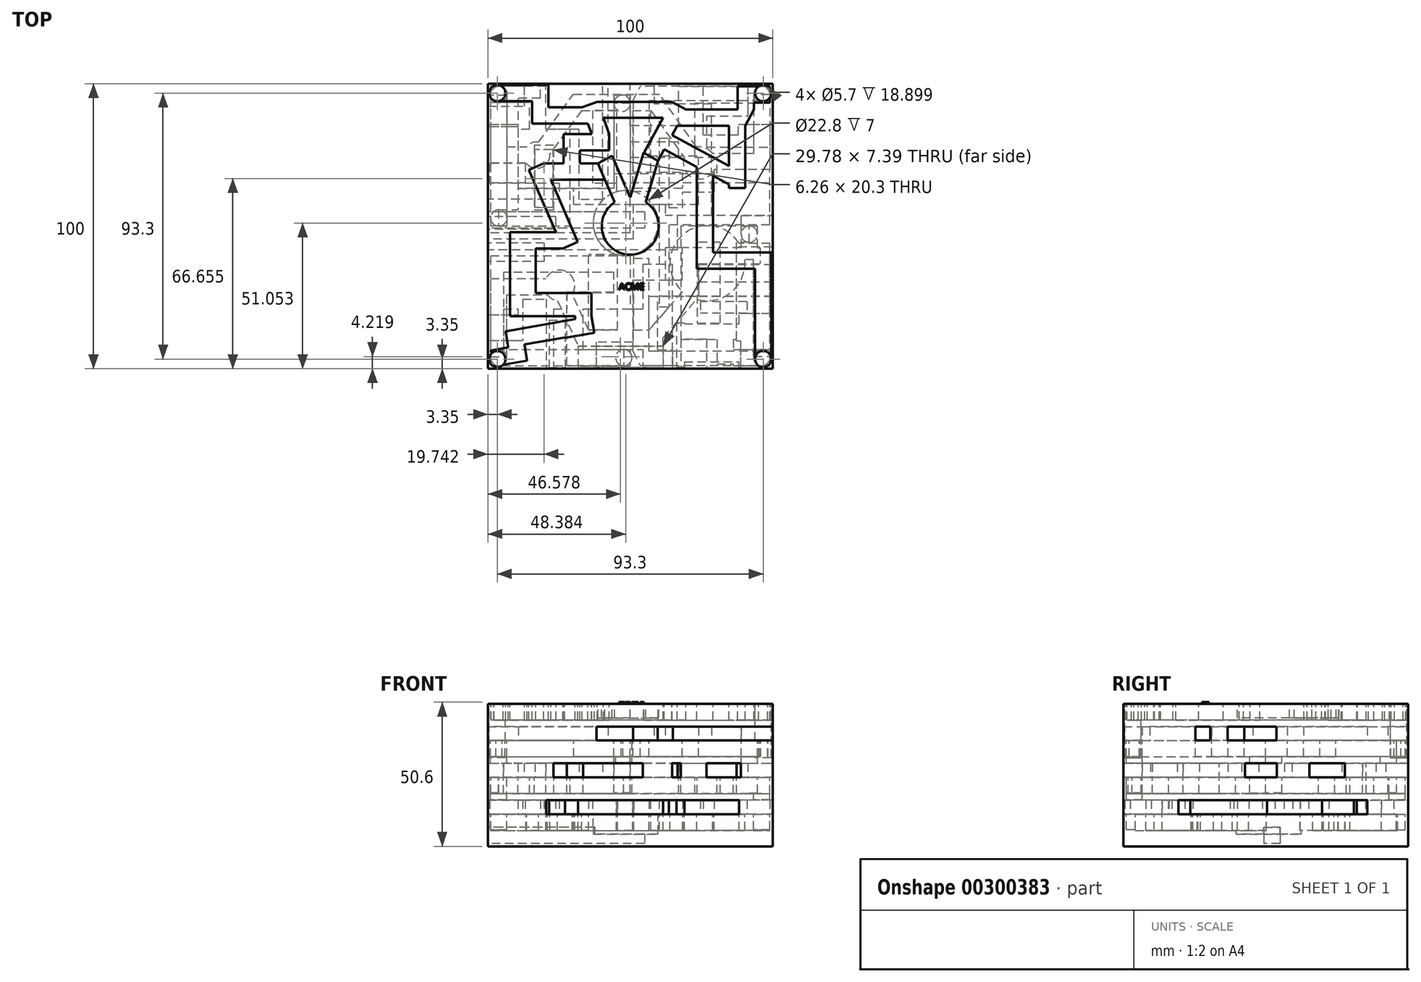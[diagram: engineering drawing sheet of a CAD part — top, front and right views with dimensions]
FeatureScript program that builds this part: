
annotation { "Feature Type Name" : "Feature", "Feature Type Description" : "" }
export const myFeature = defineFeature(function(context is Context, id is Id, definition is map)
    precondition{}
    {
        {
            var Q0;
            Q0=qCreatedBy(makeId("Top.planeOp"),FACE);
            var sketch = newSketch(context, id + "F0", { "sketchPlane" : qUnion([Q0])});
            skLineSegment(sketch, "E0.bottom", {"start": v(-50, 50) * mm, "end": v(50, 50) * mm});
            skLineSegment(sketch, "E0.top", {"start": v(-50, -50) * mm, "end": v(50, -50) * mm});
            skLineSegment(sketch, "E0.left", {"start": v(-50, 50) * mm, "end": v(-50, -50) * mm});
            skLineSegment(sketch, "E0.right", {"start": v(50, 50) * mm, "end": v(50, -50) * mm});
            skPoint(sketch, "E0.middle", {"position": v(0, 0) * mm});
            skSolve(sketch);
        }
        {
            var Q0;
            Q0 = qSketchRegion(id + "F0", true);
            extrude(context, id + "F1", {"entities" : qUnion([Q0]), "oppositeDirection" : true, "depth" : 50 * mm});
        }
        {
            var Q0;
            Q0=makeQuery(id+"F1.opExtrude","CAP_FACE",FACE,{"disambiguationData":[OSD([sQuery(id+"F0.wireOp",EDGE,"E0.bottom"),sQuery(id+"F0.wireOp",EDGE,"E0.top"),sQuery(id+"F0.wireOp",EDGE,"E0.left"),sQuery(id+"F0.wireOp",EDGE,"E0.right")])],"isStart":true});
            var sketch = newSketch(context, id + "F2", { "sketchPlane" : qUnion([Q0])});
            skCircle(sketch, "E1", {"center": v(0, 0) * mm, "radius": 10 * mm});
            skSolve(sketch);
        }
        {
            var Q0;
            Q0 = qSketchRegion(id + "F2", true);
            extrude(context, id + "F3", {"entities" : qUnion([Q0]), "operationType" : NewBodyOperationType.REMOVE, "oppositeDirection" : true, "depth" : 5 * mm});
        }
        {
            var Q0;
            Q0=makeQuery(id+"F1.opExtrude","CAP_FACE",FACE,{"disambiguationData":[OSD([sQuery(id+"F0.wireOp",EDGE,"E0.bottom"),sQuery(id+"F0.wireOp",EDGE,"E0.top"),sQuery(id+"F0.wireOp",EDGE,"E0.left"),sQuery(id+"F0.wireOp",EDGE,"E0.right")])],"isStart":true});
            var sketch = newSketch(context, id + "F4", { "sketchPlane" : qUnion([Q0])});
            skLineSegment(sketch, "E2", {"start": v(0, 10) * mm, "end": v(-6.36, 24.68) * mm});
            skLineSegment(sketch, "E3", {"start": v(0, 10) * mm, "end": v(4.66, 25.69) * mm});
            skLineSegment(sketch, "E4", {"start": v(4.66, 25.69) * mm, "end": v(9.78, 22.9) * mm});
            skLineSegment(sketch, "E5", {"start": v(9.78, 22.9) * mm, "end": v(5.46, 8.38) * mm});
            skLineSegment(sketch, "E6", {"start": v(5.46, 8.38) * mm, "end": v(0, 10) * mm});
            skLineSegment(sketch, "E7", {"start": v(-6.36, 24.68) * mm, "end": v(-11.36, 21.94) * mm});
            skLineSegment(sketch, "E8", {"start": v(-11.36, 21.94) * mm, "end": v(-5.46, 8.38) * mm});
            skLineSegment(sketch, "E9", {"start": v(-5.46, 8.38) * mm, "end": v(0, 10) * mm});
            skSolve(sketch);
        }
        {
            var Q0;
            Q0 = qSketchRegion(id + "F4", true);
            extrude(context, id + "F5", {"entities" : qUnion([Q0]), "operationType" : NewBodyOperationType.REMOVE, "oppositeDirection" : true, "depth" : 5 * mm});
        }
        {
            var Q0;
            Q0=makeQuery(id+"F1.opExtrude","CAP_FACE",FACE,{"disambiguationData":[OSD([sQuery(id+"F0.wireOp",EDGE,"E0.bottom"),sQuery(id+"F0.wireOp",EDGE,"E0.top"),sQuery(id+"F0.wireOp",EDGE,"E0.left"),sQuery(id+"F0.wireOp",EDGE,"E0.right")])],"isStart":true});
            var sketch = newSketch(context, id + "F6", { "sketchPlane" : qUnion([Q0])});
            skLineSegment(sketch, "E10.bottom", {"start": v(-11.36, 21.94) * mm, "end": v(-30.36, 21.94) * mm});
            skLineSegment(sketch, "E10.top", {"start": v(-8.88, 16.24) * mm, "end": v(-27.88, 16.24) * mm});
            skLineSegment(sketch, "E10.left", {"start": v(-11.36, 21.94) * mm, "end": v(-8.88, 16.24) * mm});
            skLineSegment(sketch, "E10.right", {"start": v(-30.36, 21.94) * mm, "end": v(-27.88, 16.24) * mm});
            skLineSegment(sketch, "E11.bottom", {"start": v(-23.36, 21.94) * mm, "end": v(-17.66, 21.94) * mm});
            skLineSegment(sketch, "E11.top", {"start": v(-23.36, 32.25) * mm, "end": v(-17.66, 32.25) * mm});
            skLineSegment(sketch, "E11.left", {"start": v(-23.36, 21.94) * mm, "end": v(-23.36, 32.25) * mm});
            skLineSegment(sketch, "E11.right", {"start": v(-17.66, 21.94) * mm, "end": v(-17.66, 32.25) * mm});
            skLineSegment(sketch, "E12.bottom", {"start": v(-17.66, 32.25) * mm, "end": v(-7.41, 32.25) * mm});
            skLineSegment(sketch, "E12.top", {"start": v(-17.66, 26.55) * mm, "end": v(-7.41, 26.55) * mm});
            skLineSegment(sketch, "E12.left", {"start": v(-17.66, 32.25) * mm, "end": v(-17.66, 26.55) * mm});
            skLineSegment(sketch, "E12.right", {"start": v(-7.41, 32.25) * mm, "end": v(-7.41, 26.55) * mm});
            skLineSegment(sketch, "E13.bottom", {"start": v(-7.41, 32.25) * mm, "end": v(-12.77, 30.3) * mm});
            skLineSegment(sketch, "E13.top", {"start": v(-11.56, 43.65) * mm, "end": v(-16.92, 41.7) * mm});
            skLineSegment(sketch, "E13.left", {"start": v(-7.41, 32.25) * mm, "end": v(-11.56, 43.65) * mm});
            skLineSegment(sketch, "E13.right", {"start": v(-12.77, 30.3) * mm, "end": v(-16.92, 41.7) * mm});
            skLineSegment(sketch, "E14.bottom", {"start": v(-16.92, 41.7) * mm, "end": v(-31.14, 41.7) * mm});
            skLineSegment(sketch, "E14.top", {"start": v(-14.84, 36) * mm, "end": v(-29.06, 36) * mm});
            skLineSegment(sketch, "E14.left", {"start": v(-16.92, 41.7) * mm, "end": v(-14.84, 36) * mm});
            skLineSegment(sketch, "E14.right", {"start": v(-31.14, 41.7) * mm, "end": v(-29.06, 36) * mm});
            skLineSegment(sketch, "E15.bottom", {"start": v(-28.72, 36) * mm, "end": v(-34.42, 36) * mm});
            skLineSegment(sketch, "E15.top", {"start": v(-28.72, 49.5) * mm, "end": v(-34.42, 49.5) * mm});
            skLineSegment(sketch, "E15.left", {"start": v(-28.72, 36) * mm, "end": v(-28.72, 49.5) * mm});
            skLineSegment(sketch, "E15.right", {"start": v(-34.42, 36) * mm, "end": v(-34.42, 49.5) * mm});
            skLineSegment(sketch, "E16.bottom", {"start": v(-47.8, 49.5) * mm, "end": v(-34.42, 49.5) * mm});
            skLineSegment(sketch, "E16.top", {"start": v(-47.8, 43.8) * mm, "end": v(-34.42, 43.8) * mm});
            skLineSegment(sketch, "E16.left", {"start": v(-47.8, 49.5) * mm, "end": v(-47.8, 43.8) * mm});
            skLineSegment(sketch, "E16.right", {"start": v(-34.42, 49.5) * mm, "end": v(-34.42, 43.8) * mm});
            skLineSegment(sketch, "E17.bottom", {"start": v(-30.36, 21.94) * mm, "end": v(-35.59, 19.66) * mm});
            skLineSegment(sketch, "E17.top", {"start": v(-18.4, -5.57) * mm, "end": v(-23.62, -7.85) * mm});
            skLineSegment(sketch, "E17.left", {"start": v(-30.36, 21.94) * mm, "end": v(-18.4, -5.57) * mm});
            skLineSegment(sketch, "E17.right", {"start": v(-35.59, 19.66) * mm, "end": v(-23.62, -7.85) * mm});
            skLineSegment(sketch, "E18.bottom", {"start": v(-23.62, -7.85) * mm, "end": v(-42.16, -7.85) * mm});
            skLineSegment(sketch, "E18.top", {"start": v(-23.62, -2.15) * mm, "end": v(-42.16, -2.15) * mm});
            skLineSegment(sketch, "E18.left", {"start": v(-23.62, -7.85) * mm, "end": v(-23.62, -2.15) * mm});
            skLineSegment(sketch, "E18.right", {"start": v(-42.16, -7.85) * mm, "end": v(-42.16, -2.15) * mm});
            skLineSegment(sketch, "E19.bottom", {"start": v(-42.16, -7.85) * mm, "end": v(-33.16, -7.85) * mm});
            skLineSegment(sketch, "E19.top", {"start": v(-42.16, -31.6) * mm, "end": v(-33.16, -31.6) * mm});
            skLineSegment(sketch, "E19.left", {"start": v(-42.16, -7.85) * mm, "end": v(-42.16, -31.6) * mm});
            skLineSegment(sketch, "E19.right", {"start": v(-33.16, -7.85) * mm, "end": v(-33.16, -31.6) * mm});
            skLineSegment(sketch, "E20.bottom", {"start": v(-33.16, -23.52) * mm, "end": v(-13.61, -23.52) * mm});
            skLineSegment(sketch, "E20.top", {"start": v(-33.16, -31.6) * mm, "end": v(-13.61, -31.6) * mm});
            skLineSegment(sketch, "E20.left", {"start": v(-33.16, -23.52) * mm, "end": v(-33.16, -31.6) * mm});
            skLineSegment(sketch, "E20.right", {"start": v(-13.61, -23.52) * mm, "end": v(-13.61, -31.6) * mm});
            skLineSegment(sketch, "E21.bottom", {"start": v(-13.61, -31.6) * mm, "end": v(-24.04, -33.45) * mm});
            skLineSegment(sketch, "E21.top", {"start": v(-12.58, -37.43) * mm, "end": v(-23.02, -39.27) * mm});
            skLineSegment(sketch, "E21.left", {"start": v(-13.61, -31.6) * mm, "end": v(-12.58, -37.43) * mm});
            skLineSegment(sketch, "E21.right", {"start": v(-24.04, -33.45) * mm, "end": v(-23.02, -39.27) * mm});
            skLineSegment(sketch, "E22.bottom", {"start": v(-13.61, -31.6) * mm, "end": v(-19.31, -31.6) * mm});
            skLineSegment(sketch, "E22.top", {"start": v(-13.61, -32.61) * mm, "end": v(-19.31, -32.61) * mm});
            skLineSegment(sketch, "E22.left", {"start": v(-13.61, -31.6) * mm, "end": v(-13.61, -32.61) * mm});
            skLineSegment(sketch, "E22.right", {"start": v(-19.31, -31.6) * mm, "end": v(-19.31, -32.61) * mm});
            skLineSegment(sketch, "E23.bottom", {"start": v(-24.04, -33.45) * mm, "end": v(-43.78, -36.92) * mm});
            skLineSegment(sketch, "E23.top", {"start": v(-23.05, -39.06) * mm, "end": v(-42.79, -42.54) * mm});
            skLineSegment(sketch, "E23.left", {"start": v(-24.04, -33.45) * mm, "end": v(-23.05, -39.06) * mm});
            skLineSegment(sketch, "E23.right", {"start": v(-43.78, -36.92) * mm, "end": v(-42.79, -42.54) * mm});
            skLineSegment(sketch, "E24.bottom", {"start": v(-42.79, -42.54) * mm, "end": v(-37.17, -41.55) * mm});
            skLineSegment(sketch, "E24.top", {"start": v(-41.8, -48.15) * mm, "end": v(-36.18, -47.16) * mm});
            skLineSegment(sketch, "E24.left", {"start": v(-42.79, -42.54) * mm, "end": v(-41.8, -48.15) * mm});
            skLineSegment(sketch, "E24.right", {"start": v(-37.17, -41.55) * mm, "end": v(-36.18, -47.16) * mm});
            skLineSegment(sketch, "E25.bottom", {"start": v(-41.8, -48.15) * mm, "end": v(-47.94, -49.24) * mm});
            skLineSegment(sketch, "E25.top", {"start": v(-42.79, -42.54) * mm, "end": v(-48.93, -43.62) * mm});
            skLineSegment(sketch, "E25.left", {"start": v(-41.8, -48.15) * mm, "end": v(-42.79, -42.54) * mm});
            skLineSegment(sketch, "E25.right", {"start": v(-47.94, -49.24) * mm, "end": v(-48.93, -43.62) * mm});
            skLineSegment(sketch, "E26.bottom", {"start": v(9.78, 22.9) * mm, "end": v(19.57, 40.93) * mm});
            skLineSegment(sketch, "E26.top", {"start": v(4.77, 25.63) * mm, "end": v(14.56, 43.65) * mm});
            skLineSegment(sketch, "E26.left", {"start": v(9.78, 22.9) * mm, "end": v(4.77, 25.63) * mm});
            skLineSegment(sketch, "E26.right", {"start": v(19.57, 40.93) * mm, "end": v(14.56, 43.65) * mm});
            skPoint(sketch, "E27.oppositeSnap0", {"position": v(-9.49, 37.95) * mm});
            skLineSegment(sketch, "E27.bottom", {"start": v(14.56, 43.65) * mm, "end": v(-11.56, 43.65) * mm});
            skLineSegment(sketch, "E27.top", {"start": v(11.47, 37.95) * mm, "end": v(-9.49, 37.95) * mm});
            skLineSegment(sketch, "E27.left", {"start": v(14.56, 43.65) * mm, "end": v(11.47, 37.95) * mm});
            skLineSegment(sketch, "E27.right", {"start": v(-11.56, 43.65) * mm, "end": v(-9.49, 37.95) * mm});
            skLineSegment(sketch, "E28.bottom", {"start": v(19.57, 40.93) * mm, "end": v(43.44, 40.93) * mm});
            skLineSegment(sketch, "E28.top", {"start": v(16.47, 35.23) * mm, "end": v(40.35, 35.23) * mm});
            skLineSegment(sketch, "E28.left", {"start": v(19.57, 40.93) * mm, "end": v(16.47, 35.23) * mm});
            skLineSegment(sketch, "E28.right", {"start": v(43.44, 40.93) * mm, "end": v(40.35, 35.23) * mm});
            skLineSegment(sketch, "E29.bottom", {"start": v(40.35, 35.23) * mm, "end": v(34.65, 35.23) * mm});
            skLineSegment(sketch, "E29.top", {"start": v(40.35, 13.41) * mm, "end": v(34.65, 13.41) * mm});
            skLineSegment(sketch, "E29.left", {"start": v(40.35, 35.23) * mm, "end": v(40.35, 13.41) * mm});
            skLineSegment(sketch, "E29.right", {"start": v(34.65, 35.23) * mm, "end": v(34.65, 13.41) * mm});
            skLineSegment(sketch, "E30.bottom", {"start": v(14.68, 31.92) * mm, "end": v(37.37, 19.6) * mm});
            skLineSegment(sketch, "E30.top", {"start": v(11.96, 26.9) * mm, "end": v(34.65, 14.59) * mm});
            skLineSegment(sketch, "E30.left", {"start": v(14.68, 31.92) * mm, "end": v(11.96, 26.9) * mm});
            skLineSegment(sketch, "E30.right", {"start": v(37.37, 19.6) * mm, "end": v(34.65, 14.59) * mm});
            skLineSegment(sketch, "E31.bottom", {"start": v(23.3, 20.75) * mm, "end": v(29, 17.65) * mm});
            skLineSegment(sketch, "E31.top", {"start": v(23.3, -14.96) * mm, "end": v(29, -14.96) * mm});
            skLineSegment(sketch, "E31.left", {"start": v(23.3, 20.75) * mm, "end": v(23.3, -14.96) * mm});
            skLineSegment(sketch, "E31.right", {"start": v(29, 17.65) * mm, "end": v(29, -14.96) * mm});
            skLineSegment(sketch, "E32.bottom", {"start": v(29, -14.96) * mm, "end": v(29, -9.26) * mm});
            skLineSegment(sketch, "E32.top", {"start": v(49.5, -14.96) * mm, "end": v(49.5, -9.26) * mm});
            skLineSegment(sketch, "E32.left", {"start": v(29, -14.96) * mm, "end": v(49.5, -14.96) * mm});
            skLineSegment(sketch, "E32.right", {"start": v(29, -9.26) * mm, "end": v(49.5, -9.26) * mm});
            skLineSegment(sketch, "E33.bottom", {"start": v(43.8, -14.96) * mm, "end": v(49.5, -14.96) * mm});
            skLineSegment(sketch, "E33.top", {"start": v(43.8, -46.22) * mm, "end": v(49.5, -46.22) * mm});
            skLineSegment(sketch, "E33.left", {"start": v(43.8, -14.96) * mm, "end": v(43.8, -46.22) * mm});
            skLineSegment(sketch, "E33.right", {"start": v(49.5, -14.96) * mm, "end": v(49.5, -46.22) * mm});
            skLineSegment(sketch, "E34.bottom", {"start": v(43.44, 40.93) * mm, "end": v(37.74, 40.93) * mm});
            skLineSegment(sketch, "E34.top", {"start": v(43.44, 49.03) * mm, "end": v(37.74, 49.03) * mm});
            skLineSegment(sketch, "E34.left", {"start": v(43.44, 40.93) * mm, "end": v(43.44, 49.03) * mm});
            skLineSegment(sketch, "E34.right", {"start": v(37.74, 40.93) * mm, "end": v(37.74, 49.03) * mm});
            skLineSegment(sketch, "E35.bottom", {"start": v(43.44, 49.03) * mm, "end": v(49.05, 49.03) * mm});
            skLineSegment(sketch, "E35.top", {"start": v(43.44, 43.33) * mm, "end": v(49.05, 43.33) * mm});
            skLineSegment(sketch, "E35.left", {"start": v(43.44, 49.03) * mm, "end": v(43.44, 43.33) * mm});
            skLineSegment(sketch, "E35.right", {"start": v(49.05, 49.03) * mm, "end": v(49.05, 43.33) * mm});
            skSolve(sketch);
        }
        {
            var Q0;
            {var subQ14=sQuery(id+"F6.wireOp",EDGE,"E10.top");Q0=makeQuery(id+"F6.imprint","IMPRINT",FACE,{"disambiguationData":[TD([[makeQuery(id+"F6.imprint","IMPRINT",EDGE,{"derivedFrom":subQ14}),1.0]])]});}
            var sketch = newSketch(context, id + "F7", { "sketchPlane" : qUnion([Q0])});
            skCircle(sketch, "E36", {"center": v(-46.65, 46.65) * mm, "radius": 2.85 * mm});
            skCircle(sketch, "E37", {"center": v(-46.65, -46.65) * mm, "radius": 2.85 * mm});
            skCircle(sketch, "E38", {"center": v(46.65, -46.65) * mm, "radius": 2.85 * mm});
            skCircle(sketch, "E39", {"center": v(46.65, 46.65) * mm, "radius": 2.85 * mm});
            skSolve(sketch);
        }
        {
            var Q0;
            Q0 = qSketchRegion(id + "F6", true);
            extrude(context, id + "F8", {"entities" : qUnion([Q0]), "operationType" : NewBodyOperationType.REMOVE, "oppositeDirection" : true, "depth" : 5.7 * mm});
        }
        {
            var Q0;
            {var subQ16=sQuery(id+"F6.wireOp",EDGE,"E10.top");Q0=makeQuery(id+"F7.imprint","IMPRINT",FACE,{"disambiguationData":[TD([[makeQuery(id+"F7.imprint","IMPRINT",EDGE,{"derivedFrom":makeQuery(id+"F6.imprint","IMPRINT",EDGE,{"derivedFrom":subQ16})}),1.0]])]});}
            var sketch = newSketch(context, id + "F9", { "sketchPlane" : qUnion([Q0])});
            skText(sketch, "E40", { "text": "ACME", "fontName": "OpenSans-Regular.ttf"});
            const initialGuessF9  = {"E40": [-0.004, -0.02238, 1, 0, 0.00238]};
            skSetInitialGuess(sketch, initialGuessF9);
            skSolve(sketch);
        }
        {
            var Q0;
            Q0 = qSketchRegion(id + "F9", true);
            extrude(context, id + "F10", {"entities" : qUnion([Q0]), "operationType" : NewBodyOperationType.ADD, "depth" : 0.6 * mm});
        }
        {
            var Q0;
            Q0=makeQuery(id+"F1.opExtrude","SWEPT_FACE",FACE,{"disambiguationData":[OSD([sQuery(id+"F0.wireOp",EDGE,"E0.top")])]});
            var sketch = newSketch(context, id + "F11", { "sketchPlane" : qUnion([Q0])});
            skLineSegment(sketch, "E41.bottom", {"start": v(-50, -8) * mm, "end": v(50, -8) * mm});
            skLineSegment(sketch, "E41.top", {"start": v(-50, -12.9) * mm, "end": v(50, -12.9) * mm});
            skLineSegment(sketch, "E41.left", {"start": v(-50, -8) * mm, "end": v(-50, -12.9) * mm});
            skLineSegment(sketch, "E41.right", {"start": v(50, -8) * mm, "end": v(50, -12.9) * mm});
            skSolve(sketch);
        }
        {
            var Q0;
            Q0 = qSketchRegion(id + "F11", true);
            extrude(context, id + "F12", {"entities" : qUnion([Q0]), "operationType" : NewBodyOperationType.REMOVE, "endBound" : BoundingType.THROUGH_ALL, "oppositeDirection" : true, "depth" : 25 * mm});
        }
        {
            var Q0;
            Q0=makeQuery(id+"F12.boolean.opBoolean","COPY",FACE,{"derivedFrom":makeQuery(id+"F12.opExtrude","SWEPT_FACE",FACE,{"disambiguationData":[OSD([sQuery(id+"F11.wireOp",EDGE,"E41.top")])]})});
            var sketch = newSketch(context, id + "F13", { "sketchPlane" : qUnion([Q0])});
            skCircle(sketch, "E42", {"center": v(-46.65, -46.65) * mm, "radius": 2.85 * mm});
            skCircle(sketch, "E43.MirrorC", {"center": v(46.65, -46.65) * mm, "radius": 2.85 * mm});
            skCircle(sketch, "E44.MirrorC", {"center": v(-46.65, 46.65) * mm, "radius": 2.85 * mm});
            skCircle(sketch, "E45.MirrorC", {"center": v(46.65, 46.65) * mm, "radius": 2.85 * mm});
            skSolve(sketch);
        }
        {
            var Q0;
            Q0 = qSketchRegion(id + "F13", true);
            extrude(context, id + "F14", {"entities" : qUnion([Q0]), "operationType" : NewBodyOperationType.REMOVE, "oppositeDirection" : true, "depth" : 6 * mm});
        }
        {
            var Q0;
            Q0=makeQuery(id+"F12.boolean.opBoolean","COPY",FACE,{"derivedFrom":makeQuery(id+"F12.opExtrude","SWEPT_FACE",FACE,{"disambiguationData":[OSD([sQuery(id+"F11.wireOp",EDGE,"E41.top")])]})});
            var sketch = newSketch(context, id + "F15", { "sketchPlane" : qUnion([Q0])});
            skLineSegment(sketch, "E46.bottom", {"start": v(45.8, -43.93) * mm, "end": v(0.93, -43.93) * mm});
            skLineSegment(sketch, "E46.top", {"start": v(48.4, -49) * mm, "end": v(3.54, -49) * mm});
            skLineSegment(sketch, "E46.left", {"start": v(45.8, -43.93) * mm, "end": v(48.4, -49) * mm});
            skLineSegment(sketch, "E46.right", {"start": v(0.93, -43.93) * mm, "end": v(3.54, -49) * mm});
            skLineSegment(sketch, "E47.MirrorCS", {"start": v(45.8, 43.93) * mm, "end": v(0.93, 43.93) * mm});
            skLineSegment(sketch, "E48.MirrorCS", {"start": v(45.8, 43.93) * mm, "end": v(48.4, 49) * mm});
            skLineSegment(sketch, "E49.MirrorCS", {"start": v(48.4, 49) * mm, "end": v(3.54, 49) * mm});
            skLineSegment(sketch, "E50.MirrorCS", {"start": v(0.93, 43.93) * mm, "end": v(3.54, 49) * mm});
            skLineSegment(sketch, "E51.bottom", {"start": v(0.93, -43.93) * mm, "end": v(6.63, -43.93) * mm});
            skLineSegment(sketch, "E51.top", {"start": v(0.93, -18.93) * mm, "end": v(6.63, -18.93) * mm});
            skLineSegment(sketch, "E51.left", {"start": v(0.93, -43.93) * mm, "end": v(0.93, -18.93) * mm});
            skLineSegment(sketch, "E51.right", {"start": v(6.63, -43.93) * mm, "end": v(6.63, -18.93) * mm});
            skLineSegment(sketch, "E52.bottom", {"start": v(6.63, -18.93) * mm, "end": v(23.97, -18.93) * mm});
            skLineSegment(sketch, "E52.top", {"start": v(6.63, -24.63) * mm, "end": v(23.97, -24.63) * mm});
            skLineSegment(sketch, "E52.left", {"start": v(6.63, -18.93) * mm, "end": v(6.63, -24.63) * mm});
            skLineSegment(sketch, "E52.right", {"start": v(23.97, -18.93) * mm, "end": v(23.97, -24.63) * mm});
            skLineSegment(sketch, "E53.MirrorCS", {"start": v(6.63, 18.93) * mm, "end": v(23.97, 18.93) * mm});
            skLineSegment(sketch, "E54.MirrorCS", {"start": v(6.63, 24.63) * mm, "end": v(23.97, 24.63) * mm});
            skLineSegment(sketch, "E55.MirrorCS", {"start": v(23.97, 18.93) * mm, "end": v(23.97, 24.63) * mm});
            skLineSegment(sketch, "E56.MirrorCS", {"start": v(6.63, 43.93) * mm, "end": v(6.63, 18.93) * mm});
            skLineSegment(sketch, "E57.MirrorCS", {"start": v(0.93, 43.93) * mm, "end": v(0.93, 18.93) * mm});
            skLineSegment(sketch, "E58.MirrorCS", {"start": v(0.93, 18.93) * mm, "end": v(6.63, 18.93) * mm});
            skLineSegment(sketch, "E59.MirrorCS", {"start": v(0.93, 43.93) * mm, "end": v(6.63, 43.93) * mm});
            skLineSegment(sketch, "E60.bottom", {"start": v(23.97, -18.93) * mm, "end": v(18.27, -18.93) * mm});
            skLineSegment(sketch, "E60.top", {"start": v(23.97, -7.53) * mm, "end": v(18.27, -7.53) * mm});
            skLineSegment(sketch, "E60.left", {"start": v(23.97, -18.93) * mm, "end": v(23.97, -7.53) * mm});
            skLineSegment(sketch, "E60.right", {"start": v(18.27, -18.93) * mm, "end": v(18.27, -7.53) * mm});
            skLineSegment(sketch, "E61.left", {"start": v(18.27, -7.53) * mm, "end": v(18.27, -13.23) * mm});
            skLineSegment(sketch, "E62.MirrorCS", {"start": v(18.27, 18.93) * mm, "end": v(18.27, 7.53) * mm});
            skLineSegment(sketch, "E63.MirrorCS", {"start": v(23.97, 18.93) * mm, "end": v(23.97, 7.53) * mm});
            skLineSegment(sketch, "E64.MirrorCS", {"start": v(23.97, 7.53) * mm, "end": v(18.27, 7.53) * mm});
            skLineSegment(sketch, "E65.MirrorCS", {"start": v(18.27, 7.53) * mm, "end": v(-19.9, 7.53) * mm});
            skLineSegment(sketch, "E66.MirrorCS", {"start": v(18.27, 13.23) * mm, "end": v(-19.9, 13.23) * mm});
            skLineSegment(sketch, "E67.MirrorCS", {"start": v(0, 45.93) * mm, "end": v(-5.7, 45.93) * mm});
            skLineSegment(sketch, "E68.MirrorCS", {"start": v(-5.7, 45.93) * mm, "end": v(-5.7, 8.83) * mm});
            skLineSegment(sketch, "E69.MirrorCS", {"start": v(0, 45.93) * mm, "end": v(0, 8.83) * mm});
            skLineSegment(sketch, "E70.MirrorCS", {"start": v(0, 8.83) * mm, "end": v(-5.7, 8.83) * mm});
            skPoint(sketch, "E71.oppositeSnap0", {"position": v(23.97, -13.23) * mm});
            skLineSegment(sketch, "E71.bottom", {"start": v(23.97, -7.53) * mm, "end": v(45.56, -7.53) * mm});
            skLineSegment(sketch, "E71.top", {"start": v(23.97, -13.23) * mm, "end": v(45.56, -13.23) * mm});
            skLineSegment(sketch, "E71.left", {"start": v(23.97, -7.53) * mm, "end": v(23.97, -13.23) * mm});
            skLineSegment(sketch, "E71.right", {"start": v(45.56, -7.53) * mm, "end": v(45.56, -13.23) * mm});
            skLineSegment(sketch, "E72.bottom", {"start": v(38.91, -7.53) * mm, "end": v(44.61, -7.53) * mm});
            skLineSegment(sketch, "E72.top", {"start": v(38.91, 0) * mm, "end": v(44.61, 0) * mm});
            skLineSegment(sketch, "E72.left", {"start": v(38.91, -7.53) * mm, "end": v(38.91, 0) * mm});
            skLineSegment(sketch, "E72.right", {"start": v(44.61, -7.53) * mm, "end": v(44.61, 0) * mm});
            skLineSegment(sketch, "E73", {"start": v(-19.9, 7.53) * mm, "end": v(-19.9, 13.23) * mm});
            skPoint(sketch, "E74.oppositeSnap0", {"position": v(0, -50) * mm});
            skLineSegment(sketch, "E74.bottom", {"start": v(-46.46, -43.3) * mm, "end": v(0, -43.3) * mm});
            skLineSegment(sketch, "E74.top", {"start": v(-46.46, -49) * mm, "end": v(0, -49) * mm});
            skLineSegment(sketch, "E74.left", {"start": v(-46.46, -43.3) * mm, "end": v(-46.46, -49) * mm});
            skLineSegment(sketch, "E74.right", {"start": v(0, -43.3) * mm, "end": v(0, -49) * mm});
            skLineSegment(sketch, "E75.bottom", {"start": v(-43.3, 47.45) * mm, "end": v(-49, 47.45) * mm});
            skLineSegment(sketch, "E75.top", {"start": v(-43.3, 0) * mm, "end": v(-49, 0) * mm});
            skLineSegment(sketch, "E75.left", {"start": v(-43.3, 47.45) * mm, "end": v(-43.3, 0) * mm});
            skLineSegment(sketch, "E75.right", {"start": v(-49, 47.45) * mm, "end": v(-49, 0) * mm});
            skLineSegment(sketch, "E76", {"start": v(-46.46, -43.3) * mm, "end": v(-47.15, -43.3) * mm});
            skLineSegment(sketch, "E77", {"start": v(-47.15, -43.3) * mm, "end": v(-47.15, -43.84) * mm});
            skLineSegment(sketch, "E78", {"start": v(-47.15, -43.84) * mm, "end": v(-46.46, -43.8) * mm});
            skLineSegment(sketch, "E79", {"start": v(44.66, -49) * mm, "end": v(45.6, -49.3) * mm});
            skLineSegment(sketch, "E80", {"start": v(45.6, -49.3) * mm, "end": v(45.6, -49) * mm});
            skLineSegment(sketch, "E81", {"start": v(44.99, -43.93) * mm, "end": v(46.24, -44.8) * mm});
            skSolve(sketch);
        }
        {
            var Q0;
            Q0 = qSketchRegion(id + "F15", true);
            var Q1;
            Q1 = qSketchRegion(id + "F17", true);
            extrude(context, id + "F16", {"entities" : qUnion([Q0, Q1]), "operationType" : NewBodyOperationType.REMOVE, "oppositeDirection" : true, "depth" : 5.7 * mm});
        }
        {
            var Q0;
            Q0=makeQuery(id+"F12.boolean.opBoolean","COPY",FACE,{"derivedFrom":makeQuery(id+"F12.opExtrude","SWEPT_FACE",FACE,{"disambiguationData":[OSD([sQuery(id+"F11.wireOp",EDGE,"E41.top")])]})});
            var sketch = newSketch(context, id + "F17", { "sketchPlane" : qUnion([Q0])});
            skCircle(sketch, "E82", {"center": v(-2.26, -46.15) * mm, "radius": 2.85 * mm});
            skPoint(sketch, "E82.first.point", {"position": v(0, -43.3) * mm});
            skPoint(sketch, "E82.second.point", {"position": v(-2.26, -49) * mm});
            skPoint(sketch, "E82.third.point", {"position": v(-2.26, -43.3) * mm});
            skCircle(sketch, "E83", {"center": v(41.76, -2.85) * mm, "radius": 2.85 * mm});
            skCircle(sketch, "E84", {"center": v(-46.15, 2.85) * mm, "radius": 2.85 * mm});
            skPoint(sketch, "E84.first.point", {"position": v(-43.3, 2.85) * mm});
            skPoint(sketch, "E84.second.point", {"position": v(-46.15, 0) * mm});
            skPoint(sketch, "E84.third.point", {"position": v(-49, 2.85) * mm});
            skCircle(sketch, "E85", {"center": v(-2.85, 43.1) * mm, "radius": 2.85 * mm});
            skPoint(sketch, "E85.first.point", {"position": v(0, 43.1) * mm});
            skPoint(sketch, "E85.second.point", {"position": v(-5.7, 43.1) * mm});
            skPoint(sketch, "E85.third.point", {"position": v(-3.16, 45.93) * mm});
            skSolve(sketch);
        }
        {
            var Q0;
            {var subQ2=sQuery(id+"F0.wireOp",EDGE,"E0.top");Q0=makeQuery(id+"F12.boolean.opBoolean","SPLIT",FACE,{"disambiguationData":[TD([makeQuery(id+"F12.opExtrude","SWEPT_FACE",FACE,{"disambiguationData":[OSD([sQuery(id+"F11.wireOp",EDGE,"E41.top")])]})])],"derivedFrom":makeQuery(id+"F1.opExtrude","SWEPT_FACE",FACE,{"disambiguationData":[OSD([subQ2])]})});}
            var sketch = newSketch(context, id + "F18", { "sketchPlane" : qUnion([Q0])});
            skLineSegment(sketch, "E86.bottom", {"start": v(-50, -12.9) * mm, "end": v(50, -12.9) * mm});
            skLineSegment(sketch, "E86.top", {"start": v(-50, -20.9) * mm, "end": v(50, -20.9) * mm});
            skLineSegment(sketch, "E86.left", {"start": v(-50, -12.9) * mm, "end": v(-50, -20.9) * mm});
            skLineSegment(sketch, "E86.right", {"start": v(50, -12.9) * mm, "end": v(50, -20.9) * mm});
            skSolve(sketch);
        }
        {
            var Q0;
            {var subQ0=sQuery(id+"F18.wireOp",EDGE,"E86.top");Q0=makeQuery(id+"F18.imprint","IMPRINT",FACE,{"disambiguationData":[TD([[makeQuery(id+"F18.imprint","IMPRINT",EDGE,{"derivedFrom":subQ0}),-1.0]])]});}
            var sketch = newSketch(context, id + "F19", { "sketchPlane" : qUnion([Q0])});
            skLineSegment(sketch, "E87.bottom", {"start": v(-50, -20.84) * mm, "end": v(50, -20.84) * mm});
            skLineSegment(sketch, "E87.top", {"start": v(-50, -25.8) * mm, "end": v(50, -25.8) * mm});
            skLineSegment(sketch, "E87.left", {"start": v(-50, -20.84) * mm, "end": v(-50, -25.8) * mm});
            skLineSegment(sketch, "E87.right", {"start": v(50, -20.84) * mm, "end": v(50, -25.8) * mm});
            skSolve(sketch);
        }
        {
            var Q0;
            Q0 = qSketchRegion(id + "F17", true);
            extrude(context, id + "F20", {"entities" : qUnion([Q0]), "operationType" : NewBodyOperationType.REMOVE, "oppositeDirection" : true, "depth" : 18.4 * mm});
        }
        {
            var Q0;
            Q0 = qSketchRegion(id + "F19", true);
            extrude(context, id + "F21", {"entities" : qUnion([Q0]), "operationType" : NewBodyOperationType.REMOVE, "endBound" : BoundingType.THROUGH_ALL, "oppositeDirection" : true, "depth" : 25 * mm});
        }
        {
            var Q0;
            Q0=makeQuery(id+"F21.boolean.opBoolean","COPY",FACE,{"derivedFrom":makeQuery(id+"F21.opExtrude","SWEPT_FACE",FACE,{"disambiguationData":[OSD([sQuery(id+"F19.wireOp",EDGE,"E87.top")])]})});
            var sketch = newSketch(context, id + "F22", { "sketchPlane" : qUnion([Q0])});
            skLineSegment(sketch, "E88.bottom", {"start": v(-2.28, -43.3) * mm, "end": v(-22.26, -43.3) * mm});
            skLineSegment(sketch, "E88.top", {"start": v(-2.28, -49) * mm, "end": v(-22.26, -49) * mm});
            skLineSegment(sketch, "E88.left", {"start": v(-2.28, -43.3) * mm, "end": v(-2.28, -49) * mm});
            skLineSegment(sketch, "E88.right", {"start": v(-22.26, -43.3) * mm, "end": v(-22.26, -49) * mm});
            skLineSegment(sketch, "E89.bottom", {"start": v(-22.26, -43.3) * mm, "end": v(-16.56, -43.3) * mm});
            skLineSegment(sketch, "E89.top", {"start": v(-22.26, -23.37) * mm, "end": v(-16.56, -23.37) * mm});
            skLineSegment(sketch, "E89.left", {"start": v(-22.26, -43.3) * mm, "end": v(-22.26, -23.37) * mm});
            skLineSegment(sketch, "E89.right", {"start": v(-16.56, -43.3) * mm, "end": v(-16.56, -23.37) * mm});
            skLineSegment(sketch, "E90.bottom", {"start": v(-16.56, -23.37) * mm, "end": v(0, -23.37) * mm});
            skLineSegment(sketch, "E90.top", {"start": v(-16.56, -29.07) * mm, "end": v(0, -29.07) * mm});
            skLineSegment(sketch, "E90.left", {"start": v(-16.56, -23.37) * mm, "end": v(-16.56, -29.07) * mm});
            skLineSegment(sketch, "E90.right", {"start": v(0, -23.37) * mm, "end": v(0, -29.07) * mm});
            skLineSegment(sketch, "E91.bottom", {"start": v(0, -23.37) * mm, "end": v(-5.7, -23.37) * mm});
            skLineSegment(sketch, "E91.top", {"start": v(0, -10.57) * mm, "end": v(-5.7, -10.57) * mm});
            skLineSegment(sketch, "E91.left", {"start": v(0, -23.37) * mm, "end": v(0, -10.57) * mm});
            skLineSegment(sketch, "E91.right", {"start": v(-5.7, -23.37) * mm, "end": v(-5.7, -10.57) * mm});
            skLineSegment(sketch, "E92.bottom", {"start": v(-5.7, -10.57) * mm, "end": v(-49, -10.57) * mm});
            skLineSegment(sketch, "E92.top", {"start": v(-5.7, -16.27) * mm, "end": v(-49, -16.27) * mm});
            skLineSegment(sketch, "E92.left", {"start": v(-5.7, -10.57) * mm, "end": v(-5.7, -16.27) * mm});
            skLineSegment(sketch, "E92.right", {"start": v(-49, -10.57) * mm, "end": v(-49, -16.27) * mm});
            skLineSegment(sketch, "E93.bottom", {"start": v(-49, -16.27) * mm, "end": v(-44.54, -16.27) * mm});
            skLineSegment(sketch, "E93.top", {"start": v(-49, -46.88) * mm, "end": v(-44.54, -46.88) * mm});
            skLineSegment(sketch, "E93.left", {"start": v(-49, -16.27) * mm, "end": v(-49, -46.88) * mm});
            skLineSegment(sketch, "E93.right", {"start": v(-44.54, -16.27) * mm, "end": v(-44.54, -46.88) * mm});
            skLineSegment(sketch, "E94.bottom", {"start": v(41.76, -5.7) * mm, "end": v(17.8, -5.7) * mm});
            skLineSegment(sketch, "E94.top", {"start": v(41.76, 0) * mm, "end": v(17.8, 0) * mm});
            skLineSegment(sketch, "E94.left", {"start": v(41.76, -5.7) * mm, "end": v(41.76, 0) * mm});
            skLineSegment(sketch, "E94.right", {"start": v(17.8, -5.7) * mm, "end": v(17.8, 0) * mm});
            skLineSegment(sketch, "E95.bottom", {"start": v(17.8, -5.7) * mm, "end": v(23.5, -5.7) * mm});
            skLineSegment(sketch, "E95.top", {"start": v(17.8, -39.76) * mm, "end": v(23.5, -39.76) * mm});
            skLineSegment(sketch, "E95.left", {"start": v(17.8, -5.7) * mm, "end": v(17.8, -39.76) * mm});
            skLineSegment(sketch, "E95.right", {"start": v(23.5, -5.7) * mm, "end": v(23.5, -39.76) * mm});
            skLineSegment(sketch, "E96.bottom", {"start": v(23.5, -39.76) * mm, "end": v(37.34, -39.76) * mm});
            skLineSegment(sketch, "E96.top", {"start": v(23.5, -34.06) * mm, "end": v(37.34, -34.06) * mm});
            skLineSegment(sketch, "E96.left", {"start": v(23.5, -39.76) * mm, "end": v(23.5, -34.06) * mm});
            skLineSegment(sketch, "E96.right", {"start": v(37.34, -39.76) * mm, "end": v(37.34, -34.06) * mm});
            skLineSegment(sketch, "E97.bottom", {"start": v(30.42, -39.76) * mm, "end": v(36.12, -39.76) * mm});
            skLineSegment(sketch, "E97.top", {"start": v(30.42, -48.3) * mm, "end": v(36.12, -48.3) * mm});
            skLineSegment(sketch, "E97.left", {"start": v(30.42, -39.76) * mm, "end": v(30.42, -48.3) * mm});
            skLineSegment(sketch, "E97.right", {"start": v(36.12, -39.76) * mm, "end": v(36.12, -48.3) * mm});
            skLineSegment(sketch, "E98.bottom", {"start": v(37.34, -34.06) * mm, "end": v(31.64, -34.06) * mm});
            skLineSegment(sketch, "E98.top", {"start": v(37.34, -5.7) * mm, "end": v(31.64, -5.7) * mm});
            skLineSegment(sketch, "E98.left", {"start": v(37.34, -34.06) * mm, "end": v(37.34, -5.7) * mm});
            skLineSegment(sketch, "E98.right", {"start": v(31.64, -34.06) * mm, "end": v(31.64, -5.7) * mm});
            skLineSegment(sketch, "E99.bottom", {"start": v(36.12, -49) * mm, "end": v(49, -49) * mm});
            skLineSegment(sketch, "E99.top", {"start": v(36.12, -43.3) * mm, "end": v(49, -43.3) * mm});
            skLineSegment(sketch, "E99.left", {"start": v(36.12, -49) * mm, "end": v(36.12, -43.3) * mm});
            skLineSegment(sketch, "E99.right", {"start": v(49, -49) * mm, "end": v(49, -43.3) * mm});
            skPoint(sketch, "E100.firstSnap0", {"position": v(0, 50) * mm});
            skLineSegment(sketch, "E100.bottom", {"start": v(0, 43.1) * mm, "end": v(-5.68, 43.1) * mm});
            skLineSegment(sketch, "E100.top", {"start": v(0, 37.9) * mm, "end": v(-5.68, 37.9) * mm});
            skLineSegment(sketch, "E100.left", {"start": v(0, 43.1) * mm, "end": v(0, 37.9) * mm});
            skLineSegment(sketch, "E100.right", {"start": v(-5.68, 43.1) * mm, "end": v(-5.68, 37.9) * mm});
            skLineSegment(sketch, "E101.bottom", {"start": v(0, 37.9) * mm, "end": v(-5.7, 37.9) * mm});
            skLineSegment(sketch, "E101.top", {"start": v(0, 18.47) * mm, "end": v(-5.7, 18.47) * mm});
            skLineSegment(sketch, "E101.left", {"start": v(0, 37.9) * mm, "end": v(0, 18.47) * mm});
            skLineSegment(sketch, "E101.right", {"start": v(-5.7, 37.9) * mm, "end": v(-5.7, 18.47) * mm});
            skLineSegment(sketch, "E102.bottom", {"start": v(0, 18.47) * mm, "end": v(30.48, 18.47) * mm});
            skLineSegment(sketch, "E102.top", {"start": v(0, 24.17) * mm, "end": v(30.48, 24.17) * mm});
            skLineSegment(sketch, "E102.left", {"start": v(0, 18.47) * mm, "end": v(0, 24.17) * mm});
            skLineSegment(sketch, "E102.right", {"start": v(30.48, 18.47) * mm, "end": v(30.48, 24.17) * mm});
            skLineSegment(sketch, "E103.bottom", {"start": v(22.67, 24.17) * mm, "end": v(16.97, 24.17) * mm});
            skLineSegment(sketch, "E103.top", {"start": v(22.67, 49) * mm, "end": v(16.97, 49) * mm});
            skLineSegment(sketch, "E103.left", {"start": v(22.67, 24.17) * mm, "end": v(22.67, 49) * mm});
            skLineSegment(sketch, "E103.right", {"start": v(16.97, 24.17) * mm, "end": v(16.97, 49) * mm});
            skLineSegment(sketch, "E104.bottom", {"start": v(16.97, 29.49) * mm, "end": v(0, 29.49) * mm});
            skLineSegment(sketch, "E104.top", {"start": v(16.97, 35.19) * mm, "end": v(0, 35.19) * mm});
            skLineSegment(sketch, "E104.left", {"start": v(16.97, 29.49) * mm, "end": v(16.97, 35.19) * mm});
            skLineSegment(sketch, "E104.right", {"start": v(0, 29.49) * mm, "end": v(0, 35.19) * mm});
            skLineSegment(sketch, "E105.bottom", {"start": v(22.67, 49) * mm, "end": v(49, 49) * mm});
            skLineSegment(sketch, "E105.top", {"start": v(22.67, 43.25) * mm, "end": v(49, 43.25) * mm});
            skLineSegment(sketch, "E105.left", {"start": v(22.67, 49) * mm, "end": v(22.67, 43.25) * mm});
            skLineSegment(sketch, "E105.right", {"start": v(49, 49) * mm, "end": v(49, 43.25) * mm});
            skLineSegment(sketch, "E106.bottom", {"start": v(-46.2, 5.7) * mm, "end": v(-21.16, 5.7) * mm});
            skLineSegment(sketch, "E106.top", {"start": v(-46.2, 0) * mm, "end": v(-21.16, 0) * mm});
            skLineSegment(sketch, "E106.left", {"start": v(-46.2, 5.7) * mm, "end": v(-46.2, 0) * mm});
            skLineSegment(sketch, "E106.right", {"start": v(-21.16, 5.7) * mm, "end": v(-21.16, 0) * mm});
            skLineSegment(sketch, "E107.bottom", {"start": v(-21.16, 5.7) * mm, "end": v(-26.86, 5.7) * mm});
            skLineSegment(sketch, "E107.top", {"start": v(-21.16, 34) * mm, "end": v(-26.86, 34) * mm});
            skLineSegment(sketch, "E107.left", {"start": v(-21.16, 5.7) * mm, "end": v(-21.16, 34) * mm});
            skLineSegment(sketch, "E107.right", {"start": v(-26.86, 5.7) * mm, "end": v(-26.86, 34) * mm});
            skLineSegment(sketch, "E108.bottom", {"start": v(-26.86, 34) * mm, "end": v(-39.38, 34) * mm});
            skLineSegment(sketch, "E108.top", {"start": v(-26.86, 28.3) * mm, "end": v(-39.38, 28.3) * mm});
            skLineSegment(sketch, "E108.left", {"start": v(-26.86, 34) * mm, "end": v(-26.86, 28.3) * mm});
            skLineSegment(sketch, "E108.right", {"start": v(-39.38, 34) * mm, "end": v(-39.38, 28.3) * mm});
            skLineSegment(sketch, "E109.bottom", {"start": v(-39.38, 28.3) * mm, "end": v(-33.68, 28.3) * mm});
            skLineSegment(sketch, "E109.top", {"start": v(-39.38, 5.7) * mm, "end": v(-33.68, 5.7) * mm});
            skLineSegment(sketch, "E109.left", {"start": v(-39.38, 28.3) * mm, "end": v(-39.38, 5.7) * mm});
            skLineSegment(sketch, "E109.right", {"start": v(-33.68, 28.3) * mm, "end": v(-33.68, 5.7) * mm});
            skLineSegment(sketch, "E110.bottom", {"start": v(-29.6, 34) * mm, "end": v(-35.3, 34) * mm});
            skLineSegment(sketch, "E110.top", {"start": v(-29.6, 49) * mm, "end": v(-35.3, 49) * mm});
            skLineSegment(sketch, "E110.left", {"start": v(-29.6, 34) * mm, "end": v(-29.6, 49) * mm});
            skLineSegment(sketch, "E110.right", {"start": v(-35.3, 34) * mm, "end": v(-35.3, 49) * mm});
            skLineSegment(sketch, "E111.bottom", {"start": v(-35.3, 49) * mm, "end": v(-49, 49) * mm});
            skLineSegment(sketch, "E111.top", {"start": v(-35.3, 43.3) * mm, "end": v(-49, 43.3) * mm});
            skLineSegment(sketch, "E111.left", {"start": v(-35.3, 49) * mm, "end": v(-35.3, 43.3) * mm});
            skLineSegment(sketch, "E111.right", {"start": v(-49, 49) * mm, "end": v(-49, 43.3) * mm});
            skSolve(sketch);
        }
        {
            var Q0;
            Q0=makeQuery(id+"F21.boolean.opBoolean","COPY",FACE,{"derivedFrom":makeQuery(id+"F21.opExtrude","SWEPT_FACE",FACE,{"disambiguationData":[OSD([sQuery(id+"F19.wireOp",EDGE,"E87.top")])]})});
            var sketch = newSketch(context, id + "F23", { "sketchPlane" : qUnion([Q0])});
            skCircle(sketch, "E112", {"center": v(-46.15, 46.15) * mm, "radius": 2.85 * mm});
            skCircle(sketch, "E113.MirrorC", {"center": v(-46.15, -46.15) * mm, "radius": 2.85 * mm});
            skCircle(sketch, "E114.MirrorC", {"center": v(46.15, 46.15) * mm, "radius": 2.85 * mm});
            skCircle(sketch, "E115.MirrorC", {"center": v(46.15, -46.15) * mm, "radius": 2.85 * mm});
            skSolve(sketch);
        }
        {
            var Q0;
            Q0 = qSketchRegion(id + "F22", true);
            extrude(context, id + "F24", {"entities" : qUnion([Q0]), "operationType" : NewBodyOperationType.REMOVE, "oppositeDirection" : true, "depth" : 5.7 * mm});
        }
        {
            var Q0;
            Q0 = qSketchRegion(id + "F23", true);
            extrude(context, id + "F25", {"entities" : qUnion([Q0]), "operationType" : NewBodyOperationType.REMOVE, "oppositeDirection" : true, "depth" : 18.4 * mm});
        }
        {
            var Q0;
            {var subQ2=sQuery(id+"F0.wireOp",EDGE,"E0.top");Q0=makeQuery(id+"F21.boolean.opBoolean","SPLIT",FACE,{"disambiguationData":[TD([makeQuery(id+"F21.opExtrude","SWEPT_FACE",FACE,{"disambiguationData":[OSD([sQuery(id+"F19.wireOp",EDGE,"E87.top")])]})])],"derivedFrom":makeQuery(id+"F12.boolean.opBoolean","SPLIT",FACE,{"disambiguationData":[TD([makeQuery(id+"F12.opExtrude","SWEPT_FACE",FACE,{"disambiguationData":[OSD([sQuery(id+"F11.wireOp",EDGE,"E41.top")])]})])],"derivedFrom":makeQuery(id+"F1.opExtrude","SWEPT_FACE",FACE,{"disambiguationData":[OSD([subQ2])]})})});}
            var sketch = newSketch(context, id + "F26", { "sketchPlane" : qUnion([Q0])});
            skLineSegment(sketch, "E116.bottom", {"start": v(-50, -25.8) * mm, "end": v(50, -25.8) * mm});
            skLineSegment(sketch, "E116.top", {"start": v(-50, -33.8) * mm, "end": v(50, -33.8) * mm});
            skLineSegment(sketch, "E116.left", {"start": v(-50, -25.8) * mm, "end": v(-50, -33.8) * mm});
            skLineSegment(sketch, "E116.right", {"start": v(50, -25.8) * mm, "end": v(50, -33.8) * mm});
            skSolve(sketch);
        }
        {
            var Q0;
            {var subQ0=sQuery(id+"F26.wireOp",EDGE,"E116.top");Q0=makeQuery(id+"F26.imprint","IMPRINT",FACE,{"disambiguationData":[TD([[makeQuery(id+"F26.imprint","IMPRINT",EDGE,{"derivedFrom":subQ0}),-1.0]])]});}
            var sketch = newSketch(context, id + "F27", { "sketchPlane" : qUnion([Q0])});
            skLineSegment(sketch, "E117.bottom", {"start": v(-50, -33.8) * mm, "end": v(50, -33.8) * mm});
            skLineSegment(sketch, "E117.top", {"start": v(-50, -38.7) * mm, "end": v(50, -38.7) * mm});
            skLineSegment(sketch, "E117.left", {"start": v(-50, -33.8) * mm, "end": v(-50, -38.7) * mm});
            skLineSegment(sketch, "E117.right", {"start": v(50, -33.8) * mm, "end": v(50, -38.7) * mm});
            skSolve(sketch);
        }
        {
            var Q0;
            Q0 = qSketchRegion(id + "F27", true);
            extrude(context, id + "F28", {"entities" : qUnion([Q0]), "operationType" : NewBodyOperationType.REMOVE, "endBound" : BoundingType.THROUGH_ALL, "oppositeDirection" : true, "depth" : 25 * mm});
        }
        {
            var Q0;
            Q0=makeQuery(id+"F28.boolean.opBoolean","COPY",FACE,{"derivedFrom":makeQuery(id+"F28.opExtrude","SWEPT_FACE",FACE,{"disambiguationData":[OSD([sQuery(id+"F27.wireOp",EDGE,"E117.top")])]})});
            var sketch = newSketch(context, id + "F29", { "sketchPlane" : qUnion([Q0])});
            skLineSegment(sketch, "E118.bottom", {"start": v(-48.98, -45.8) * mm, "end": v(-43.28, -45.8) * mm});
            skLineSegment(sketch, "E118.top", {"start": v(-48.98, -18.38) * mm, "end": v(-43.28, -18.38) * mm});
            skLineSegment(sketch, "E118.left", {"start": v(-48.98, -45.8) * mm, "end": v(-48.98, -18.38) * mm});
            skLineSegment(sketch, "E118.right", {"start": v(-43.28, -45.8) * mm, "end": v(-43.28, -18.38) * mm});
            skLineSegment(sketch, "E119.bottom", {"start": v(43.33, -45.73) * mm, "end": v(49.03, -45.73) * mm});
            skLineSegment(sketch, "E119.top", {"start": v(43.33, -6.05) * mm, "end": v(49.03, -6.05) * mm});
            skLineSegment(sketch, "E119.left", {"start": v(43.33, -45.73) * mm, "end": v(43.33, -6.05) * mm});
            skLineSegment(sketch, "E119.right", {"start": v(49.03, -45.73) * mm, "end": v(49.03, -6.05) * mm});
            skLineSegment(sketch, "E120.bottom", {"start": v(49, 46.07) * mm, "end": v(43.3, 46.07) * mm});
            skLineSegment(sketch, "E120.top", {"start": v(49, 19.78) * mm, "end": v(43.3, 19.78) * mm});
            skLineSegment(sketch, "E120.left", {"start": v(49, 46.07) * mm, "end": v(49, 19.78) * mm});
            skLineSegment(sketch, "E120.right", {"start": v(43.3, 46.07) * mm, "end": v(43.3, 19.78) * mm});
            skLineSegment(sketch, "E121.bottom", {"start": v(-43.32, 45.84) * mm, "end": v(-49.02, 45.84) * mm});
            skLineSegment(sketch, "E121.top", {"start": v(-43.32, 22.18) * mm, "end": v(-49.02, 22.18) * mm});
            skLineSegment(sketch, "E121.left", {"start": v(-43.32, 45.84) * mm, "end": v(-43.32, 22.18) * mm});
            skLineSegment(sketch, "E121.right", {"start": v(-49.02, 45.84) * mm, "end": v(-49.02, 22.18) * mm});
            skLineSegment(sketch, "E122.bottom", {"start": v(-43.32, 22.18) * mm, "end": v(-34.41, 22.18) * mm});
            skLineSegment(sketch, "E122.top", {"start": v(-43.32, 27.88) * mm, "end": v(-34.41, 27.88) * mm});
            skLineSegment(sketch, "E122.left", {"start": v(-43.32, 22.18) * mm, "end": v(-43.32, 27.88) * mm});
            skLineSegment(sketch, "E122.right", {"start": v(-34.41, 22.18) * mm, "end": v(-34.41, 27.88) * mm});
            skCircle(sketch, "E123", {"center": v(-32.83, 24.91) * mm, "radius": 4.62 * mm});
            skPoint(sketch, "E123.first.point", {"position": v(-36.37, 27.88) * mm});
            skPoint(sketch, "E123.second.point", {"position": v(-36.56, 22.18) * mm});
            skPoint(sketch, "E123.third.point", {"position": v(-28.23, 25.25) * mm});
            skLineSegment(sketch, "E124.bottom", {"start": v(43.3, 19.78) * mm, "end": v(27.85, 19.78) * mm});
            skLineSegment(sketch, "E124.top", {"start": v(43.3, 25.48) * mm, "end": v(27.85, 25.48) * mm});
            skLineSegment(sketch, "E124.left", {"start": v(43.3, 19.78) * mm, "end": v(43.3, 25.48) * mm});
            skLineSegment(sketch, "E124.right", {"start": v(27.85, 19.78) * mm, "end": v(27.85, 25.48) * mm});
            skCircle(sketch, "E125", {"center": v(24.3, 22.15) * mm, "radius": 5.64 * mm});
            skPoint(sketch, "E125.first.point", {"position": v(28.86, 25.48) * mm});
            skPoint(sketch, "E125.second.point", {"position": v(29.43, 19.78) * mm});
            skPoint(sketch, "E125.third.point", {"position": v(19.2, 24.55) * mm});
            skLineSegment(sketch, "E126.bottom", {"start": v(43.33, -6.05) * mm, "end": v(37.18, -6.05) * mm});
            skLineSegment(sketch, "E126.top", {"start": v(43.33, -11.75) * mm, "end": v(37.18, -11.75) * mm});
            skLineSegment(sketch, "E126.left", {"start": v(43.33, -6.05) * mm, "end": v(43.33, -11.75) * mm});
            skLineSegment(sketch, "E126.right", {"start": v(37.18, -6.05) * mm, "end": v(37.18, -11.75) * mm});
            skCircle(sketch, "E127", {"center": v(27.07, -13.01) * mm, "radius": 13.17 * mm});
            skPoint(sketch, "E127.first.point", {"position": v(38.24, -6.05) * mm});
            skPoint(sketch, "E127.second.point", {"position": v(40.17, -11.75) * mm});
            skPoint(sketch, "E127.third.point", {"position": v(14.38, -16.52) * mm});
            skLineSegment(sketch, "E128.bottom", {"start": v(-43.28, -18.38) * mm, "end": v(-27.67, -18.38) * mm});
            skLineSegment(sketch, "E128.top", {"start": v(-43.28, -24.08) * mm, "end": v(-27.67, -24.08) * mm});
            skLineSegment(sketch, "E128.left", {"start": v(-43.28, -18.38) * mm, "end": v(-43.28, -24.08) * mm});
            skLineSegment(sketch, "E128.right", {"start": v(-27.67, -18.38) * mm, "end": v(-27.67, -24.08) * mm});
            skCircle(sketch, "E129", {"center": v(-24.83, -20.83) * mm, "radius": 5.35 * mm});
            skPoint(sketch, "E129.first.point", {"position": v(-29.59, -18.38) * mm});
            skPoint(sketch, "E129.second.point", {"position": v(-29.08, -24.08) * mm});
            skPoint(sketch, "E129.third.point", {"position": v(-19.5, -20.46) * mm});
            skLineSegment(sketch, "E130", {"start": v(-32.13, 29.48) * mm, "end": v(-19.97, 46.28) * mm});
            skLineSegment(sketch, "E131", {"start": v(-19.97, 46.28) * mm, "end": v(-15.35, 42.93) * mm});
            skLineSegment(sketch, "E132", {"start": v(-15.35, 42.93) * mm, "end": v(-28.23, 25.32) * mm});
            skLineSegment(sketch, "E133", {"start": v(-28.23, 25.32) * mm, "end": v(-32.13, 29.48) * mm});
            skLineSegment(sketch, "E134", {"start": v(23.3, 27.7) * mm, "end": v(10.2, 46.28) * mm});
            skLineSegment(sketch, "E135", {"start": v(10.2, 46.28) * mm, "end": v(5.53, 43) * mm});
            skLineSegment(sketch, "E136", {"start": v(5.53, 43) * mm, "end": v(18.97, 23.98) * mm});
            skLineSegment(sketch, "E137", {"start": v(18.97, 23.98) * mm, "end": v(23.3, 27.7) * mm});
            skLineSegment(sketch, "E138.bottom", {"start": v(-19.97, 46.28) * mm, "end": v(10.19, 46.28) * mm});
            skLineSegment(sketch, "E138.top", {"start": v(-19.97, 40.58) * mm, "end": v(10.19, 40.58) * mm});
            skLineSegment(sketch, "E138.left", {"start": v(-19.97, 46.28) * mm, "end": v(-19.97, 40.58) * mm});
            skLineSegment(sketch, "E138.right", {"start": v(10.19, 46.28) * mm, "end": v(10.19, 40.58) * mm});
            skLineSegment(sketch, "E139", {"start": v(-25.55, -26.13) * mm, "end": v(-18.32, -42.06) * mm});
            skLineSegment(sketch, "E140", {"start": v(-18.32, -42.06) * mm, "end": v(-13.13, -39.7) * mm});
            skLineSegment(sketch, "E141", {"start": v(-13.13, -39.7) * mm, "end": v(-20.36, -23.77) * mm});
            skLineSegment(sketch, "E142", {"start": v(-20.36, -23.77) * mm, "end": v(-25.55, -26.13) * mm});
            skLineSegment(sketch, "E143", {"start": v(18.37, -22.9) * mm, "end": v(6.56, -36.36) * mm});
            skLineSegment(sketch, "E144", {"start": v(6.56, -36.36) * mm, "end": v(11.55, -39.12) * mm});
            skLineSegment(sketch, "E145", {"start": v(11.55, -39.12) * mm, "end": v(23.36, -25.65) * mm});
            skLineSegment(sketch, "E146", {"start": v(23.36, -25.65) * mm, "end": v(18.37, -22.9) * mm});
            skLineSegment(sketch, "E147.bottom", {"start": v(-18.32, -42.06) * mm, "end": v(11.55, -42.06) * mm});
            skLineSegment(sketch, "E147.top", {"start": v(-18.32, -36.36) * mm, "end": v(11.55, -36.36) * mm});
            skLineSegment(sketch, "E147.left", {"start": v(-18.32, -42.06) * mm, "end": v(-18.32, -36.36) * mm});
            skLineSegment(sketch, "E147.right", {"start": v(11.55, -42.06) * mm, "end": v(11.55, -36.36) * mm});
            skLineSegment(sketch, "E148.bottom", {"start": v(-4.9, 40.58) * mm, "end": v(0.8, 40.58) * mm});
            skLineSegment(sketch, "E148.top", {"start": v(-4.9, 7.22) * mm, "end": v(0.8, 7.22) * mm});
            skLineSegment(sketch, "E148.left", {"start": v(-4.9, 40.58) * mm, "end": v(-4.9, 7.22) * mm});
            skLineSegment(sketch, "E148.right", {"start": v(0.8, 40.58) * mm, "end": v(0.8, 7.22) * mm});
            skLineSegment(sketch, "E149.bottom", {"start": v(-4.46, -36.36) * mm, "end": v(1.24, -36.36) * mm});
            skLineSegment(sketch, "E149.top", {"start": v(-4.46, -5.52) * mm, "end": v(1.24, -5.52) * mm});
            skLineSegment(sketch, "E149.left", {"start": v(-4.46, -36.36) * mm, "end": v(-4.46, -5.52) * mm});
            skLineSegment(sketch, "E149.right", {"start": v(1.24, -36.36) * mm, "end": v(1.24, -5.52) * mm});
            skSolve(sketch);
        }
        {
            var Q0;
            Q0=makeQuery(id+"F28.boolean.opBoolean","COPY",FACE,{"derivedFrom":makeQuery(id+"F28.opExtrude","SWEPT_FACE",FACE,{"disambiguationData":[OSD([sQuery(id+"F27.wireOp",EDGE,"E117.top")])]})});
            var sketch = newSketch(context, id + "F30", { "sketchPlane" : qUnion([Q0])});
            skCircle(sketch, "E150", {"center": v(-1.62, 1.05) * mm, "radius": 11.4 * mm});
            skPoint(sketch, "E150.first.point", {"position": v(-7.13, 11.03) * mm});
            skPoint(sketch, "E150.second.point", {"position": v(2.85, -9.43) * mm});
            skPoint(sketch, "E150.third.point", {"position": v(-6.37, -9.3) * mm});
            skSolve(sketch);
        }
        {
            var Q0;
            Q0 = qSketchRegion(id + "F29", true);
            extrude(context, id + "F31", {"entities" : qUnion([Q0]), "operationType" : NewBodyOperationType.REMOVE, "oppositeDirection" : true, "depth" : 5.7 * mm});
        }
        {
            var Q0;
            Q0 = qSketchRegion(id + "F30", true);
            extrude(context, id + "F32", {"entities" : qUnion([Q0]), "operationType" : NewBodyOperationType.REMOVE, "oppositeDirection" : true, "depth" : 7 * mm});
        }
        {
            var Q0;
            {var subQ2=sQuery(id+"F0.wireOp",EDGE,"E0.left");Q0=makeQuery(id+"F28.boolean.opBoolean","SPLIT",FACE,{"disambiguationData":[TD([makeQuery(id+"F28.opExtrude","SWEPT_FACE",FACE,{"disambiguationData":[OSD([sQuery(id+"F27.wireOp",EDGE,"E117.top")])]})])],"derivedFrom":makeQuery(id+"F21.boolean.opBoolean","SPLIT",FACE,{"disambiguationData":[TD([makeQuery(id+"F21.opExtrude","SWEPT_FACE",FACE,{"disambiguationData":[OSD([sQuery(id+"F19.wireOp",EDGE,"E87.top")])]})])],"derivedFrom":makeQuery(id+"F12.boolean.opBoolean","SPLIT",FACE,{"disambiguationData":[TD([makeQuery(id+"F12.opExtrude","SWEPT_FACE",FACE,{"disambiguationData":[OSD([sQuery(id+"F11.wireOp",EDGE,"E41.top")])]})])],"derivedFrom":makeQuery(id+"F1.opExtrude","SWEPT_FACE",FACE,{"disambiguationData":[OSD([subQ2])]})})})});}
            var sketch = newSketch(context, id + "F33", { "sketchPlane" : qUnion([Q0])});
            skLineSegment(sketch, "E151.bottom", {"start": v(-5, -43.3) * mm, "end": v(0.7, -43.3) * mm});
            skLineSegment(sketch, "E151.top", {"start": v(-5, -49) * mm, "end": v(0.7, -49) * mm});
            skLineSegment(sketch, "E151.left", {"start": v(-5, -43.3) * mm, "end": v(-5, -49) * mm});
            skLineSegment(sketch, "E151.right", {"start": v(0.7, -43.3) * mm, "end": v(0.7, -49) * mm});
            skSolve(sketch);
        }
        {
            var Q0;
            Q0 = qSketchRegion(id + "F33", true);
            extrude(context, id + "F34", {"entities" : qUnion([Q0]), "operationType" : NewBodyOperationType.REMOVE, "oppositeDirection" : true, "depth" : 55 * mm});
        }
        {
            var Q0;
            Q0=makeQuery(id+"F28.boolean.opBoolean","COPY",FACE,{"derivedFrom":makeQuery(id+"F28.opExtrude","SWEPT_FACE",FACE,{"disambiguationData":[OSD([sQuery(id+"F27.wireOp",EDGE,"E117.top")])]})});
            var sketch = newSketch(context, id + "F35", { "sketchPlane" : qUnion([Q0])});
            skLineSegment(sketch, "E152.bottom", {"start": v(-24.95, 15.03) * mm, "end": v(-50, 15.03) * mm});
            skLineSegment(sketch, "E152.top", {"start": v(-24.95, 9.47) * mm, "end": v(-50, 9.47) * mm});
            skLineSegment(sketch, "E152.left", {"start": v(-24.95, 15.03) * mm, "end": v(-24.95, 9.47) * mm});
            skLineSegment(sketch, "E152.right", {"start": v(-50, 15.03) * mm, "end": v(-50, 9.47) * mm});
            skLineSegment(sketch, "E153.bottom", {"start": v(-30.22, -5.94) * mm, "end": v(-50, -5.94) * mm});
            skLineSegment(sketch, "E153.top", {"start": v(-30.22, -12.45) * mm, "end": v(-50, -12.45) * mm});
            skLineSegment(sketch, "E153.left", {"start": v(-30.22, -5.94) * mm, "end": v(-30.22, -12.45) * mm});
            skLineSegment(sketch, "E153.right", {"start": v(-50, -5.94) * mm, "end": v(-50, -12.45) * mm});
            skLineSegment(sketch, "E154.bottom", {"start": v(-26.17, 3.3) * mm, "end": v(-50, 3.3) * mm});
            skLineSegment(sketch, "E154.top", {"start": v(-26.17, -1.15) * mm, "end": v(-50, -1.15) * mm});
            skLineSegment(sketch, "E154.left", {"start": v(-26.17, 3.3) * mm, "end": v(-26.17, -1.15) * mm});
            skLineSegment(sketch, "E154.right", {"start": v(-50, 3.3) * mm, "end": v(-50, -1.15) * mm});
            skLineSegment(sketch, "E155.bottom", {"start": v(-31.57, 44.89) * mm, "end": v(-39.46, 44.89) * mm});
            skLineSegment(sketch, "E155.top", {"start": v(-31.57, 50) * mm, "end": v(-39.46, 50) * mm});
            skLineSegment(sketch, "E155.left", {"start": v(-31.57, 44.89) * mm, "end": v(-31.57, 50) * mm});
            skLineSegment(sketch, "E155.right", {"start": v(-39.46, 44.89) * mm, "end": v(-39.46, 50) * mm});
            skLineSegment(sketch, "E156.bottom", {"start": v(37.98, 31.94) * mm, "end": v(25.6, 31.94) * mm});
            skLineSegment(sketch, "E156.top", {"start": v(37.98, 50) * mm, "end": v(25.6, 50) * mm});
            skLineSegment(sketch, "E156.left", {"start": v(37.98, 31.94) * mm, "end": v(37.98, 50) * mm});
            skLineSegment(sketch, "E156.right", {"start": v(25.6, 31.94) * mm, "end": v(25.6, 50) * mm});
            skPoint(sketch, "E157.oppositeSnap0", {"position": v(49, 32.93) * mm});
            skLineSegment(sketch, "E157.bottom", {"start": v(18.37, 6.47) * mm, "end": v(49, 6.47) * mm});
            skLineSegment(sketch, "E157.top", {"start": v(18.37, 11.97) * mm, "end": v(49, 11.97) * mm});
            skLineSegment(sketch, "E157.left", {"start": v(18.37, 6.47) * mm, "end": v(18.37, 11.97) * mm});
            skLineSegment(sketch, "E157.right", {"start": v(49, 6.47) * mm, "end": v(49, 11.97) * mm});
            skLineSegment(sketch, "E158.bottom", {"start": v(18.97, -47.59) * mm, "end": v(38.24, -47.59) * mm});
            skLineSegment(sketch, "E158.top", {"start": v(18.97, -34.2) * mm, "end": v(38.24, -34.2) * mm});
            skLineSegment(sketch, "E158.left", {"start": v(18.97, -47.59) * mm, "end": v(18.97, -34.2) * mm});
            skLineSegment(sketch, "E158.right", {"start": v(38.24, -47.59) * mm, "end": v(38.24, -34.2) * mm});
            skLineSegment(sketch, "E159.bottom", {"start": v(-37.76, -25.65) * mm, "end": v(-29.5, -25.65) * mm});
            skLineSegment(sketch, "E159.top", {"start": v(-37.76, -50) * mm, "end": v(-29.5, -50) * mm});
            skLineSegment(sketch, "E159.left", {"start": v(-37.76, -25.65) * mm, "end": v(-37.76, -50) * mm});
            skLineSegment(sketch, "E159.right", {"start": v(-29.5, -25.65) * mm, "end": v(-29.5, -50) * mm});
            skSolve(sketch);
        }
        {
            var Q0;
            Q0 = qSketchRegion(id + "F35", true);
            extrude(context, id + "F36", {"entities" : qUnion([Q0]), "operationType" : NewBodyOperationType.ADD, "depth" : 5 * mm});
        }
        {
            var Q0;
            {var subQ8=makeQuery(id+"F21.opExtrude","SWEPT_FACE",FACE,{"disambiguationData":[OSD([sQuery(id+"F19.wireOp",EDGE,"E87.top")])]});Q0=makeQuery(id+"F24.boolean.opBoolean","SPLIT",FACE,{"disambiguationData":[TD([makeQuery(id+"F1.opExtrude","SWEPT_FACE",FACE,{"disambiguationData":[OSD([sQuery(id+"F0.wireOp",EDGE,"E0.bottom")])]})])],"derivedFrom":makeQuery(id+"F21.boolean.opBoolean","COPY",FACE,{"derivedFrom":subQ8})});}
            var sketch = newSketch(context, id + "F37", { "sketchPlane" : qUnion([Q0])});
            skLineSegment(sketch, "E160.bottom", {"start": v(0, 3.83) * mm, "end": v(50, 3.83) * mm});
            skLineSegment(sketch, "E160.top", {"start": v(0, 15.31) * mm, "end": v(50, 15.31) * mm});
            skLineSegment(sketch, "E160.left", {"start": v(0, 3.83) * mm, "end": v(0, 15.31) * mm});
            skLineSegment(sketch, "E160.right", {"start": v(50, 3.83) * mm, "end": v(50, 15.31) * mm});
            skLineSegment(sketch, "E161.bottom", {"start": v(26.84, 27.76) * mm, "end": v(50, 27.76) * mm});
            skLineSegment(sketch, "E161.top", {"start": v(26.84, 38.63) * mm, "end": v(50, 38.63) * mm});
            skLineSegment(sketch, "E161.left", {"start": v(26.84, 27.76) * mm, "end": v(26.84, 38.63) * mm});
            skLineSegment(sketch, "E161.right", {"start": v(50, 27.76) * mm, "end": v(50, 38.63) * mm});
            skLineSegment(sketch, "E162.bottom", {"start": v(4.45, -13.32) * mm, "end": v(14.68, -13.32) * mm});
            skLineSegment(sketch, "E162.top", {"start": v(4.45, -50) * mm, "end": v(14.68, -50) * mm});
            skLineSegment(sketch, "E162.left", {"start": v(4.45, -13.32) * mm, "end": v(4.45, -50) * mm});
            skLineSegment(sketch, "E162.right", {"start": v(14.68, -13.32) * mm, "end": v(14.68, -50) * mm});
            skLineSegment(sketch, "E163.bottom", {"start": v(-39.38, -29.07) * mm, "end": v(-26.94, -29.07) * mm});
            skLineSegment(sketch, "E163.top", {"start": v(-39.38, -50) * mm, "end": v(-26.94, -50) * mm});
            skLineSegment(sketch, "E163.left", {"start": v(-39.38, -29.07) * mm, "end": v(-39.38, -50) * mm});
            skLineSegment(sketch, "E163.right", {"start": v(-26.94, -29.07) * mm, "end": v(-26.94, -50) * mm});
            skLineSegment(sketch, "E164.bottom", {"start": v(0, -2.42) * mm, "end": v(-50, -2.42) * mm});
            skLineSegment(sketch, "E164.top", {"start": v(0, -8.38) * mm, "end": v(-50, -8.38) * mm});
            skLineSegment(sketch, "E164.left", {"start": v(0, -2.42) * mm, "end": v(0, -8.38) * mm});
            skLineSegment(sketch, "E164.right", {"start": v(-50, -2.42) * mm, "end": v(-50, -8.38) * mm});
            skLineSegment(sketch, "E165.bottom", {"start": v(-9.72, 9.24) * mm, "end": v(-18, 9.24) * mm});
            skLineSegment(sketch, "E165.top", {"start": v(-9.72, 50) * mm, "end": v(-18, 50) * mm});
            skLineSegment(sketch, "E165.left", {"start": v(-9.72, 9.24) * mm, "end": v(-9.72, 50) * mm});
            skLineSegment(sketch, "E165.right", {"start": v(-18, 9.24) * mm, "end": v(-18, 50) * mm});
            skLineSegment(sketch, "E166.bottom", {"start": v(17.8, -39.76) * mm, "end": v(26.78, -39.76) * mm});
            skLineSegment(sketch, "E166.top", {"start": v(17.8, -50) * mm, "end": v(26.78, -50) * mm});
            skLineSegment(sketch, "E166.left", {"start": v(17.8, -39.76) * mm, "end": v(17.8, -50) * mm});
            skLineSegment(sketch, "E166.right", {"start": v(26.78, -39.76) * mm, "end": v(26.78, -50) * mm});
            skSolve(sketch);
        }
        {
            var Q0;
            Q0 = qSketchRegion(id + "F37", true);
            extrude(context, id + "F38", {"entities" : qUnion([Q0]), "operationType" : NewBodyOperationType.ADD, "depth" : 5 * mm});
        }
        {
            var Q0;
            Q0=makeQuery(id+"F12.boolean.opBoolean","COPY",FACE,{"derivedFrom":makeQuery(id+"F12.opExtrude","SWEPT_FACE",FACE,{"disambiguationData":[OSD([sQuery(id+"F11.wireOp",EDGE,"E41.top")])]})});
            var sketch = newSketch(context, id + "F39", { "sketchPlane" : qUnion([Q0])});
            skLineSegment(sketch, "E167.bottom", {"start": v(28.57, 3.7) * mm, "end": v(50, 3.7) * mm});
            skLineSegment(sketch, "E167.top", {"start": v(28.57, 42.88) * mm, "end": v(50, 42.88) * mm});
            skLineSegment(sketch, "E167.left", {"start": v(28.57, 3.7) * mm, "end": v(28.57, 42.88) * mm});
            skLineSegment(sketch, "E167.right", {"start": v(50, 3.7) * mm, "end": v(50, 42.88) * mm});
            skLineSegment(sketch, "E168.bottom", {"start": v(-7.81, 13.23) * mm, "end": v(-39.26, 13.23) * mm});
            skLineSegment(sketch, "E168.top", {"start": v(-7.81, 50) * mm, "end": v(-39.26, 50) * mm});
            skLineSegment(sketch, "E168.left", {"start": v(-7.81, 13.23) * mm, "end": v(-7.81, 50) * mm});
            skLineSegment(sketch, "E168.right", {"start": v(-39.26, 13.23) * mm, "end": v(-39.26, 50) * mm});
            skLineSegment(sketch, "E169.bottom", {"start": v(0.93, -18.93) * mm, "end": v(-50, -18.93) * mm});
            skLineSegment(sketch, "E169.top", {"start": v(0.93, -4.54) * mm, "end": v(-50, -4.54) * mm});
            skLineSegment(sketch, "E169.left", {"start": v(0.93, -18.93) * mm, "end": v(0.93, -4.54) * mm});
            skLineSegment(sketch, "E169.right", {"start": v(-50, -18.93) * mm, "end": v(-50, -4.54) * mm});
            skLineSegment(sketch, "E170.top", {"start": v(0.93, -40.73) * mm, "end": v(-50, -40.73) * mm});
            skLineSegment(sketch, "E170.left", {"start": v(0.93, -18.93) * mm, "end": v(0.93, -40.73) * mm});
            skLineSegment(sketch, "E170.right", {"start": v(-50, -18.93) * mm, "end": v(-50, -40.73) * mm});
            skLineSegment(sketch, "E171.bottom", {"start": v(9.63, -43.37) * mm, "end": v(50, -43.37) * mm});
            skLineSegment(sketch, "E171.top", {"start": v(9.63, -24.63) * mm, "end": v(50, -24.63) * mm});
            skLineSegment(sketch, "E171.left", {"start": v(9.63, -43.37) * mm, "end": v(9.63, -24.63) * mm});
            skLineSegment(sketch, "E171.right", {"start": v(50, -43.37) * mm, "end": v(50, -24.63) * mm});
            skLineSegment(sketch, "E172.bottom", {"start": v(23.97, -19.49) * mm, "end": v(50, -19.49) * mm});
            skLineSegment(sketch, "E172.top", {"start": v(23.97, -13.44) * mm, "end": v(50, -13.44) * mm});
            skLineSegment(sketch, "E172.left", {"start": v(23.97, -19.49) * mm, "end": v(23.97, -13.44) * mm});
            skLineSegment(sketch, "E172.right", {"start": v(50, -19.49) * mm, "end": v(50, -13.44) * mm});
            skSolve(sketch);
        }
        {
            var Q0;
            Q0 = qSketchRegion(id + "F39", true);
            extrude(context, id + "F40", {"entities" : qUnion([Q0]), "operationType" : NewBodyOperationType.ADD, "depth" : 5 * mm});
        }
        {
            var Q0;
            {var subQ8=makeQuery(id+"F21.opExtrude","SWEPT_FACE",FACE,{"disambiguationData":[OSD([sQuery(id+"F19.wireOp",EDGE,"E87.top")])]});Q0=makeQuery(id+"F24.boolean.opBoolean","SPLIT",FACE,{"disambiguationData":[TD([makeQuery(id+"F1.opExtrude","SWEPT_FACE",FACE,{"disambiguationData":[OSD([sQuery(id+"F0.wireOp",EDGE,"E0.bottom")])]})])],"derivedFrom":makeQuery(id+"F21.boolean.opBoolean","COPY",FACE,{"derivedFrom":subQ8})});}
            var sketch = newSketch(context, id + "F41", { "sketchPlane" : qUnion([Q0])});
            skLineSegment(sketch, "E173.bottom", {"start": v(-50, -50) * mm, "end": v(-39.38, -50) * mm});
            skLineSegment(sketch, "E173.top", {"start": v(-50, -31.04) * mm, "end": v(-39.38, -31.04) * mm});
            skLineSegment(sketch, "E173.left", {"start": v(-50, -50) * mm, "end": v(-50, -31.04) * mm});
            skLineSegment(sketch, "E173.right", {"start": v(-39.38, -50) * mm, "end": v(-39.38, -31.04) * mm});
            skLineSegment(sketch, "E174.bottom", {"start": v(-50, 50) * mm, "end": v(-37.24, 50) * mm});
            skLineSegment(sketch, "E174.top", {"start": v(-50, 42.12) * mm, "end": v(-37.24, 42.12) * mm});
            skLineSegment(sketch, "E174.left", {"start": v(-50, 50) * mm, "end": v(-50, 42.12) * mm});
            skLineSegment(sketch, "E174.right", {"start": v(-37.24, 50) * mm, "end": v(-37.24, 42.12) * mm});
            skLineSegment(sketch, "E175.bottom", {"start": v(50, 50) * mm, "end": v(41.28, 50) * mm});
            skLineSegment(sketch, "E175.top", {"start": v(50, 38.63) * mm, "end": v(41.28, 38.63) * mm});
            skLineSegment(sketch, "E175.left", {"start": v(50, 50) * mm, "end": v(50, 38.63) * mm});
            skLineSegment(sketch, "E175.right", {"start": v(41.28, 50) * mm, "end": v(41.28, 38.63) * mm});
            skLineSegment(sketch, "E176.bottom", {"start": v(50, -50) * mm, "end": v(38.87, -50) * mm});
            skLineSegment(sketch, "E176.top", {"start": v(50, -40.4) * mm, "end": v(38.87, -40.4) * mm});
            skLineSegment(sketch, "E176.left", {"start": v(50, -50) * mm, "end": v(50, -40.4) * mm});
            skLineSegment(sketch, "E176.right", {"start": v(38.87, -50) * mm, "end": v(38.87, -40.4) * mm});
            skSolve(sketch);
        }
        {
            var Q0;
            Q0 = qSketchRegion(id + "F41", true);
            extrude(context, id + "F42", {"entities" : qUnion([Q0]), "operationType" : NewBodyOperationType.ADD, "depth" : 6 * mm});
        }
        {
            var Q0;
            Q0=makeQuery(id+"F28.boolean.opBoolean","COPY",FACE,{"derivedFrom":makeQuery(id+"F28.opExtrude","SWEPT_FACE",FACE,{"disambiguationData":[OSD([sQuery(id+"F27.wireOp",EDGE,"E117.top")])]})});
            var sketch = newSketch(context, id + "F43", { "sketchPlane" : qUnion([Q0])});
            skLineSegment(sketch, "E177.bottom", {"start": v(-50, -50) * mm, "end": v(-37.76, -50) * mm});
            skLineSegment(sketch, "E177.top", {"start": v(-50, -40.14) * mm, "end": v(-37.76, -40.14) * mm});
            skLineSegment(sketch, "E177.left", {"start": v(-50, -50) * mm, "end": v(-50, -40.14) * mm});
            skLineSegment(sketch, "E177.right", {"start": v(-37.76, -50) * mm, "end": v(-37.76, -40.14) * mm});
            skLineSegment(sketch, "E178.bottom", {"start": v(-50, 50) * mm, "end": v(-39.46, 50) * mm});
            skLineSegment(sketch, "E178.top", {"start": v(-50, 41.52) * mm, "end": v(-39.46, 41.52) * mm});
            skLineSegment(sketch, "E178.left", {"start": v(-50, 50) * mm, "end": v(-50, 41.52) * mm});
            skLineSegment(sketch, "E178.right", {"start": v(-39.46, 50) * mm, "end": v(-39.46, 41.52) * mm});
            skLineSegment(sketch, "E179.bottom", {"start": v(50, 50) * mm, "end": v(37.98, 50) * mm});
            skLineSegment(sketch, "E179.top", {"start": v(50, 35.65) * mm, "end": v(37.98, 35.65) * mm});
            skLineSegment(sketch, "E179.left", {"start": v(50, 50) * mm, "end": v(50, 35.65) * mm});
            skLineSegment(sketch, "E179.right", {"start": v(37.98, 50) * mm, "end": v(37.98, 35.65) * mm});
            skPoint(sketch, "E180.oppositeSnap0", {"position": v(38.24, -40.9) * mm});
            skLineSegment(sketch, "E180.bottom", {"start": v(50, -50) * mm, "end": v(38.24, -50) * mm});
            skLineSegment(sketch, "E180.top", {"start": v(50, -30.65) * mm, "end": v(38.24, -30.65) * mm});
            skLineSegment(sketch, "E180.left", {"start": v(50, -50) * mm, "end": v(50, -30.65) * mm});
            skLineSegment(sketch, "E180.right", {"start": v(38.24, -50) * mm, "end": v(38.24, -30.65) * mm});
            skLineSegment(sketch, "E181.top", {"start": v(-50, 34.95) * mm, "end": v(-39.46, 34.95) * mm});
            skLineSegment(sketch, "E181.left", {"start": v(-50, 41.52) * mm, "end": v(-50, 34.95) * mm});
            skLineSegment(sketch, "E181.right", {"start": v(-39.46, 41.52) * mm, "end": v(-39.46, 34.95) * mm});
            skSolve(sketch);
        }
        {
            var Q0;
            Q0 = qSketchRegion(id + "F43", true);
            extrude(context, id + "F44", {"entities" : qUnion([Q0]), "operationType" : NewBodyOperationType.ADD, "depth" : 5 * mm});
        }
        {
            var Q0;
            Q0=makeQuery(id+"F40.boolean.opBoolean","SPLIT",FACE,{"disambiguationData":[TD([makeQuery(id+"F1.opExtrude","SWEPT_FACE",FACE,{"disambiguationData":[OSD([sQuery(id+"F0.wireOp",EDGE,"E0.top")])]})])],"derivedFrom":makeQuery(id+"F12.boolean.opBoolean","COPY",FACE,{"derivedFrom":makeQuery(id+"F12.opExtrude","SWEPT_FACE",FACE,{"disambiguationData":[OSD([sQuery(id+"F11.wireOp",EDGE,"E41.top")])]})})});
            var sketch = newSketch(context, id + "F45", { "sketchPlane" : qUnion([Q0])});
            skLineSegment(sketch, "E182.bottom", {"start": v(-50, 50) * mm, "end": v(-39.26, 50) * mm});
            skLineSegment(sketch, "E182.top", {"start": v(-50, 35.67) * mm, "end": v(-39.26, 35.67) * mm});
            skLineSegment(sketch, "E182.left", {"start": v(-50, 50) * mm, "end": v(-50, 35.67) * mm});
            skLineSegment(sketch, "E182.right", {"start": v(-39.26, 50) * mm, "end": v(-39.26, 35.67) * mm});
            skLineSegment(sketch, "E183.bottom", {"start": v(50, 50) * mm, "end": v(42.09, 50) * mm});
            skLineSegment(sketch, "E183.top", {"start": v(50, 42.88) * mm, "end": v(42.09, 42.88) * mm});
            skLineSegment(sketch, "E183.left", {"start": v(50, 50) * mm, "end": v(50, 42.88) * mm});
            skLineSegment(sketch, "E183.right", {"start": v(42.09, 50) * mm, "end": v(42.09, 42.88) * mm});
            skLineSegment(sketch, "E184.bottom", {"start": v(42.09, 50) * mm, "end": v(8.33, 50) * mm});
            skLineSegment(sketch, "E184.top", {"start": v(42.09, 42.88) * mm, "end": v(8.33, 42.88) * mm});
            skLineSegment(sketch, "E184.right", {"start": v(8.33, 50) * mm, "end": v(8.33, 42.88) * mm});
            skLineSegment(sketch, "E185.bottom", {"start": v(50, -49.9) * mm, "end": v(14.97, -49.9) * mm});
            skLineSegment(sketch, "E185.top", {"start": v(50, -43.35) * mm, "end": v(14.97, -43.35) * mm});
            skLineSegment(sketch, "E185.left", {"start": v(50, -49.9) * mm, "end": v(50, -43.35) * mm});
            skLineSegment(sketch, "E185.right", {"start": v(14.97, -49.9) * mm, "end": v(14.97, -43.35) * mm});
            skLineSegment(sketch, "E186.bottom", {"start": v(-50, -50) * mm, "end": v(-11.89, -50) * mm});
            skLineSegment(sketch, "E186.top", {"start": v(-50, -40.73) * mm, "end": v(-11.89, -40.73) * mm});
            skLineSegment(sketch, "E186.left", {"start": v(-50, -50) * mm, "end": v(-50, -40.73) * mm});
            skLineSegment(sketch, "E186.right", {"start": v(-11.89, -50) * mm, "end": v(-11.89, -40.73) * mm});
            skSolve(sketch);
        }
        {
            var Q0;
            Q0 = qSketchRegion(id + "F45", true);
            extrude(context, id + "F46", {"entities" : qUnion([Q0]), "operationType" : NewBodyOperationType.ADD, "depth" : 5 * mm});
        }
        {
            var Q0;
            Q0 = qSketchRegion(id + "F7", true);
            extrude(context, id + "F47", {"entities" : qUnion([Q0]), "operationType" : NewBodyOperationType.REMOVE, "oppositeDirection" : true, "depth" : 12.9 * mm});
        }
        {
            var Q0;
            Q0=makeQuery(id+"F44.boolean.opBoolean","SPLIT",FACE,{"disambiguationData":[TD([makeQuery(id+"F1.opExtrude","SWEPT_FACE",FACE,{"disambiguationData":[OSD([sQuery(id+"F0.wireOp",EDGE,"E0.right")])]})])],"derivedFrom":makeQuery(id+"F28.boolean.opBoolean","COPY",FACE,{"derivedFrom":makeQuery(id+"F28.opExtrude","SWEPT_FACE",FACE,{"disambiguationData":[OSD([sQuery(id+"F27.wireOp",EDGE,"E117.top")])]})})});
            var sketch = newSketch(context, id + "F48", { "sketchPlane" : qUnion([Q0])});
            skLineSegment(sketch, "E187.bottom", {"start": v(-4.9, 40.58) * mm, "end": v(-13.18, 40.58) * mm});
            skLineSegment(sketch, "E187.top", {"start": v(-4.9, 15.03) * mm, "end": v(-13.18, 15.03) * mm});
            skLineSegment(sketch, "E187.left", {"start": v(-4.9, 40.58) * mm, "end": v(-4.9, 15.03) * mm});
            skLineSegment(sketch, "E187.right", {"start": v(-13.18, 40.58) * mm, "end": v(-13.18, 15.03) * mm});
            skLineSegment(sketch, "E188.bottom", {"start": v(-4.46, -36.36) * mm, "end": v(-14.6, -36.36) * mm});
            skLineSegment(sketch, "E188.top", {"start": v(-4.46, -9.99) * mm, "end": v(-14.6, -9.99) * mm});
            skLineSegment(sketch, "E188.left", {"start": v(-4.46, -36.36) * mm, "end": v(-4.46, -9.99) * mm});
            skLineSegment(sketch, "E188.right", {"start": v(-14.6, -36.36) * mm, "end": v(-14.6, -9.99) * mm});
            skLineSegment(sketch, "E189.bottom", {"start": v(1.24, -36.36) * mm, "end": v(6.54, -36.36) * mm});
            skLineSegment(sketch, "E189.top", {"start": v(1.24, -11.27) * mm, "end": v(6.54, -11.27) * mm});
            skLineSegment(sketch, "E189.left", {"start": v(1.24, -36.36) * mm, "end": v(1.24, -11.27) * mm});
            skLineSegment(sketch, "E189.right", {"start": v(6.54, -36.36) * mm, "end": v(6.54, -11.27) * mm});
            skLineSegment(sketch, "E190.bottom", {"start": v(0.8, 40.58) * mm, "end": v(7.06, 40.58) * mm});
            skLineSegment(sketch, "E190.top", {"start": v(0.8, 12.2) * mm, "end": v(7.06, 12.2) * mm});
            skLineSegment(sketch, "E190.left", {"start": v(0.8, 40.58) * mm, "end": v(0.8, 12.2) * mm});
            skLineSegment(sketch, "E190.right", {"start": v(7.06, 40.58) * mm, "end": v(7.06, 12.2) * mm});
            skLineSegment(sketch, "E191.bottom", {"start": v(10.16, 30.94) * mm, "end": v(13.6, 30.94) * mm});
            skLineSegment(sketch, "E191.top", {"start": v(10.16, -28.33) * mm, "end": v(13.6, -28.33) * mm});
            skLineSegment(sketch, "E191.left", {"start": v(10.16, 30.94) * mm, "end": v(10.16, -28.33) * mm});
            skLineSegment(sketch, "E191.right", {"start": v(13.6, 30.94) * mm, "end": v(13.6, -28.33) * mm});
            skLineSegment(sketch, "E192.bottom", {"start": v(49, 6.47) * mm, "end": v(13.6, 6.47) * mm});
            skLineSegment(sketch, "E192.top", {"start": v(49, 0.4) * mm, "end": v(13.6, 0.4) * mm});
            skLineSegment(sketch, "E192.left", {"start": v(49, 6.47) * mm, "end": v(49, 0.4) * mm});
            skLineSegment(sketch, "E192.right", {"start": v(13.6, 6.47) * mm, "end": v(13.6, 0.4) * mm});
            skLineSegment(sketch, "E193.bottom", {"start": v(40.95, -26.48) * mm, "end": v(24.6, -26.48) * mm});
            skLineSegment(sketch, "E193.top", {"start": v(40.95, -30.6) * mm, "end": v(24.6, -30.6) * mm});
            skLineSegment(sketch, "E193.left", {"start": v(40.95, -26.48) * mm, "end": v(40.95, -30.6) * mm});
            skLineSegment(sketch, "E193.right", {"start": v(24.6, -26.48) * mm, "end": v(24.6, -30.6) * mm});
            skLineSegment(sketch, "E194.bottom", {"start": v(29.43, 19.78) * mm, "end": v(49, 19.78) * mm});
            skLineSegment(sketch, "E194.top", {"start": v(29.43, 11.97) * mm, "end": v(49, 11.97) * mm});
            skLineSegment(sketch, "E194.left", {"start": v(29.43, 19.78) * mm, "end": v(29.43, 11.97) * mm});
            skLineSegment(sketch, "E194.right", {"start": v(49, 19.78) * mm, "end": v(49, 11.97) * mm});
            skLineSegment(sketch, "E195.bottom", {"start": v(-13.18, 29.98) * mm, "end": v(-23.18, 29.98) * mm});
            skLineSegment(sketch, "E195.top", {"start": v(-13.18, 10.03) * mm, "end": v(-29.83, 10.03) * mm});
            skLineSegment(sketch, "E195.left", {"start": v(-13.18, 29.98) * mm, "end": v(-13.18, 10.03) * mm});
            skLineSegment(sketch, "E196", {"start": v(-23.18, 29.98) * mm, "end": v(-29.83, 10.03) * mm});
            skLineSegment(sketch, "E197.bottom", {"start": v(-36.83, 22.14) * mm, "end": v(-49.24, 22.14) * mm});
            skLineSegment(sketch, "E197.top", {"start": v(-36.83, 15.1) * mm, "end": v(-49.24, 15.1) * mm});
            skLineSegment(sketch, "E197.left", {"start": v(-36.83, 22.14) * mm, "end": v(-36.83, 15.1) * mm});
            skLineSegment(sketch, "E197.right", {"start": v(-49.24, 22.14) * mm, "end": v(-49.24, 15.1) * mm});
            skLineSegment(sketch, "E198.bottom", {"start": v(-28.52, -32.98) * mm, "end": v(-22.9, -32.98) * mm});
            skLineSegment(sketch, "E198.top", {"start": v(-28.52, -49.6) * mm, "end": v(-22.9, -49.6) * mm});
            skLineSegment(sketch, "E198.left", {"start": v(-28.52, -32.98) * mm, "end": v(-28.52, -49.6) * mm});
            skLineSegment(sketch, "E198.right", {"start": v(-22.9, -32.98) * mm, "end": v(-22.9, -49.6) * mm});
            skLineSegment(sketch, "E199.bottom", {"start": v(-18.31, -42.09) * mm, "end": v(11.47, -42.09) * mm});
            skLineSegment(sketch, "E199.top", {"start": v(-18.31, -49.47) * mm, "end": v(11.47, -49.47) * mm});
            skLineSegment(sketch, "E199.left", {"start": v(-18.31, -42.09) * mm, "end": v(-18.31, -49.47) * mm});
            skLineSegment(sketch, "E199.right", {"start": v(11.47, -42.09) * mm, "end": v(11.47, -49.47) * mm});
            skLineSegment(sketch, "E200.bottom", {"start": v(18.96, -33.95) * mm, "end": v(16.25, -33.95) * mm});
            skLineSegment(sketch, "E200.top", {"start": v(18.96, -49.56) * mm, "end": v(16.25, -49.56) * mm});
            skLineSegment(sketch, "E200.left", {"start": v(18.96, -33.95) * mm, "end": v(18.96, -49.56) * mm});
            skLineSegment(sketch, "E200.right", {"start": v(16.25, -33.95) * mm, "end": v(16.25, -49.56) * mm});
            skSolve(sketch);
        }
        {
            var Q0;
            Q0=makeQuery(id+"F48.imprint","IMPRINT",FACE,{"disambiguationData":[TD([[makeQuery(id+"F48.imprint","IMPRINT",EDGE,{"derivedFrom":sQuery(id+"F48.wireOp",EDGE,"E188.bottom")}),-1.0]])]});
            var Q1;
            Q1=makeQuery(id+"F48.imprint","IMPRINT",FACE,{"disambiguationData":[TD([[makeQuery(id+"F48.imprint","IMPRINT",EDGE,{"derivedFrom":sQuery(id+"F48.wireOp",EDGE,"E193.bottom")}),1.0]])]});
            var Q2;
            {var subQ2=sQuery(id+"F48.wireOp",EDGE,"E187.bottom");Q2=makeQuery(id+"F48.imprint","IMPRINT",FACE,{"disambiguationData":[TD([[makeQuery(id+"F48.imprint","IMPRINT",EDGE,{"derivedFrom":subQ2}),1.0]])]});}
            var Q3;
            Q3=makeQuery(id+"F48.imprint","IMPRINT",FACE,{"disambiguationData":[TD([[makeQuery(id+"F48.imprint","IMPRINT",EDGE,{"derivedFrom":sQuery(id+"F48.wireOp",EDGE,"E189.bottom")}),1.0]])]});
            var Q4;
            Q4=makeQuery(id+"F48.imprint","IMPRINT",FACE,{"disambiguationData":[TD([[makeQuery(id+"F48.imprint","IMPRINT",EDGE,{"derivedFrom":sQuery(id+"F48.wireOp",EDGE,"E190.bottom")}),-1.0]])]});
            var Q5;
            {var subQ1=sQuery(id+"F48.wireOp",EDGE,"E191.bottom");Q5=makeQuery(id+"F48.imprint","IMPRINT",FACE,{"disambiguationData":[TD([[makeQuery(id+"F48.imprint","IMPRINT",EDGE,{"derivedFrom":subQ1}),-1.0]])]});}
            var Q6;
            Q6=makeQuery(id+"F48.imprint","IMPRINT",FACE,{"disambiguationData":[TD([[makeQuery(id+"F48.imprint","IMPRINT",EDGE,{"derivedFrom":sQuery(id+"F48.wireOp",EDGE,"E194.bottom")}),1.0]])]});
            var Q7;
            Q7=makeQuery(id+"F48.imprint","IMPRINT",FACE,{"disambiguationData":[TD([[makeQuery(id+"F48.imprint","IMPRINT",EDGE,{"derivedFrom":sQuery(id+"F48.wireOp",EDGE,"E192.top")}),-1.0]])]});
            var Q8;
            Q8=makeQuery(id+"F48.imprint","IMPRINT",FACE,{"disambiguationData":[TD([[makeQuery(id+"F48.imprint","IMPRINT",EDGE,{"derivedFrom":sQuery(id+"F48.wireOp",EDGE,"E197.bottom")}),1.0]])]});
            var Q9;
            Q9=makeQuery(id+"F48.imprint","IMPRINT",FACE,{"disambiguationData":[TD([[makeQuery(id+"F48.imprint","IMPRINT",EDGE,{"derivedFrom":sQuery(id+"F48.wireOp",EDGE,"E198.bottom")}),-1.0]])]});
            var Q10;
            Q10=makeQuery(id+"F48.imprint","IMPRINT",FACE,{"disambiguationData":[TD([[makeQuery(id+"F48.imprint","IMPRINT",EDGE,{"derivedFrom":sQuery(id+"F48.wireOp",EDGE,"E199.bottom")}),-1.0]])]});
            var Q11;
            Q11=makeQuery(id+"F48.imprint","IMPRINT",FACE,{"disambiguationData":[TD([[makeQuery(id+"F48.imprint","IMPRINT",EDGE,{"derivedFrom":sQuery(id+"F48.wireOp",EDGE,"E200.bottom")}),1.0]])]});
            extrude(context, id + "F49", {"entities" : qUnion([Q0, Q1, Q2, Q3, Q4, Q5, Q6, Q7, Q8, Q9, Q10, Q11]), "operationType" : NewBodyOperationType.ADD, "depth" : 6 * mm});
        }
        {
            var Q0;
            {var subQ31=makeQuery(id+"F1.opExtrude","SWEPT_FACE",FACE,{"disambiguationData":[OSD([sQuery(id+"F0.wireOp",EDGE,"E0.left")])]});var subQ60=makeQuery(id+"F12.boolean.opBoolean","COPY",FACE,{"derivedFrom":makeQuery(id+"F12.opExtrude","SWEPT_FACE",FACE,{"disambiguationData":[OSD([sQuery(id+"F11.wireOp",EDGE,"E41.top")])]})});Q0=makeQuery(id+"F46.boolean.opBoolean","SPLIT",FACE,{"disambiguationData":[TD([subQ31])],"derivedFrom":makeQuery(id+"F40.boolean.opBoolean","SPLIT",FACE,{"disambiguationData":[TD([makeQuery(id+"F1.opExtrude","SWEPT_FACE",FACE,{"disambiguationData":[OSD([sQuery(id+"F0.wireOp",EDGE,"E0.bottom")])]})])],"derivedFrom":subQ60})});}
            var sketch = newSketch(context, id + "F50", { "sketchPlane" : qUnion([Q0])});
            skPoint(sketch, "E201.firstSnap0", {"position": v(0.93, -11.74) * mm});
            skLineSegment(sketch, "E201.bottom", {"start": v(0.93, 7.53) * mm, "end": v(12.34, 7.53) * mm});
            skLineSegment(sketch, "E201.top", {"start": v(0.93, -18.93) * mm, "end": v(12.34, -18.93) * mm});
            skLineSegment(sketch, "E201.left", {"start": v(0.93, 7.53) * mm, "end": v(0.93, -18.93) * mm});
            skLineSegment(sketch, "E201.right", {"start": v(12.34, 7.53) * mm, "end": v(12.34, -18.93) * mm});
            skLineSegment(sketch, "E202.bottom", {"start": v(38.91, -7.53) * mm, "end": v(12.34, -7.53) * mm});
            skLineSegment(sketch, "E202.top", {"start": v(38.91, 3.7) * mm, "end": v(12.34, 3.7) * mm});
            skLineSegment(sketch, "E202.left", {"start": v(38.91, -7.53) * mm, "end": v(38.91, 3.7) * mm});
            skLineSegment(sketch, "E202.right", {"start": v(12.34, -7.53) * mm, "end": v(12.34, 3.7) * mm});
            skSolve(sketch);
        }
        {
            var Q0;
            Q0 = qSketchRegion(id + "F50", true);
            extrude(context, id + "F51", {"entities" : qUnion([Q0]), "operationType" : NewBodyOperationType.ADD, "depth" : 6 * mm});
        }
        {
            var Q0;
            {var subQ13=makeQuery(id+"F21.opExtrude","SWEPT_FACE",FACE,{"disambiguationData":[OSD([sQuery(id+"F19.wireOp",EDGE,"E87.top")])]});var subQ55=makeQuery(id+"F1.opExtrude","SWEPT_FACE",FACE,{"disambiguationData":[OSD([sQuery(id+"F0.wireOp",EDGE,"E0.bottom")])]});Q0=makeQuery(id+"F42.boolean.opBoolean","SPLIT",FACE,{"disambiguationData":[TD([subQ55])],"derivedFrom":makeQuery(id+"F24.boolean.opBoolean","SPLIT",FACE,{"disambiguationData":[TD([subQ55])],"derivedFrom":makeQuery(id+"F21.boolean.opBoolean","COPY",FACE,{"derivedFrom":subQ13})})});}
            var sketch = newSketch(context, id + "F52", { "sketchPlane" : qUnion([Q0])});
            skLineSegment(sketch, "E203.bottom", {"start": v(0, -8.38) * mm, "end": v(16.58, -8.38) * mm});
            skLineSegment(sketch, "E203.top", {"start": v(0, 3.83) * mm, "end": v(16.58, 3.83) * mm});
            skLineSegment(sketch, "E203.left", {"start": v(0, -8.38) * mm, "end": v(0, 3.83) * mm});
            skLineSegment(sketch, "E203.right", {"start": v(16.58, -8.38) * mm, "end": v(16.58, 3.83) * mm});
            skLineSegment(sketch, "E204.bottom", {"start": v(50, -40.4) * mm, "end": v(37.34, -40.4) * mm});
            skLineSegment(sketch, "E204.top", {"start": v(50, -7.28) * mm, "end": v(37.34, -7.28) * mm});
            skLineSegment(sketch, "E204.left", {"start": v(50, -40.4) * mm, "end": v(50, -7.28) * mm});
            skLineSegment(sketch, "E204.right", {"start": v(37.34, -40.4) * mm, "end": v(37.34, -7.28) * mm});
            skLineSegment(sketch, "E205.bottom", {"start": v(16.97, 35.19) * mm, "end": v(0, 35.19) * mm});
            skLineSegment(sketch, "E205.top", {"start": v(16.97, 50) * mm, "end": v(0, 50) * mm});
            skLineSegment(sketch, "E205.left", {"start": v(16.97, 35.19) * mm, "end": v(16.97, 50) * mm});
            skLineSegment(sketch, "E205.right", {"start": v(0, 35.19) * mm, "end": v(0, 50) * mm});
            skLineSegment(sketch, "E206.bottom", {"start": v(-29.6, 34) * mm, "end": v(-18, 34) * mm});
            skLineSegment(sketch, "E206.top", {"start": v(-29.6, 50) * mm, "end": v(-18, 50) * mm});
            skLineSegment(sketch, "E206.left", {"start": v(-29.6, 34) * mm, "end": v(-29.6, 50) * mm});
            skLineSegment(sketch, "E206.right", {"start": v(-18, 34) * mm, "end": v(-18, 50) * mm});
            skLineSegment(sketch, "E207.bottom", {"start": v(-27.13, 6.5) * mm, "end": v(-33.39, 6.5) * mm});
            skLineSegment(sketch, "E207.top", {"start": v(-27.13, 26.8) * mm, "end": v(-33.39, 26.8) * mm});
            skLineSegment(sketch, "E207.left", {"start": v(-27.13, 6.5) * mm, "end": v(-27.13, 26.8) * mm});
            skLineSegment(sketch, "E207.right", {"start": v(-33.39, 6.5) * mm, "end": v(-33.39, 26.8) * mm});
            skLineSegment(sketch, "E208.bottom", {"start": v(-5.7, -16.27) * mm, "end": v(-44.54, -16.27) * mm});
            skLineSegment(sketch, "E208.top", {"start": v(-5.7, -23.27) * mm, "end": v(-44.54, -23.27) * mm});
            skLineSegment(sketch, "E208.left", {"start": v(-5.7, -16.27) * mm, "end": v(-5.7, -23.27) * mm});
            skLineSegment(sketch, "E208.right", {"start": v(-44.54, -16.27) * mm, "end": v(-44.54, -23.27) * mm});
            skLineSegment(sketch, "E209.bottom", {"start": v(-44.54, -23.27) * mm, "end": v(-22.26, -23.27) * mm});
            skLineSegment(sketch, "E209.top", {"start": v(-44.54, -29.07) * mm, "end": v(-22.26, -29.07) * mm});
            skLineSegment(sketch, "E209.left", {"start": v(-44.54, -23.27) * mm, "end": v(-44.54, -29.07) * mm});
            skLineSegment(sketch, "E209.right", {"start": v(-22.26, -23.27) * mm, "end": v(-22.26, -29.07) * mm});
            skLineSegment(sketch, "E210.bottom", {"start": v(-16.56, -29.07) * mm, "end": v(4.45, -29.07) * mm});
            skLineSegment(sketch, "E210.top", {"start": v(-16.56, -43.3) * mm, "end": v(4.45, -43.3) * mm});
            skLineSegment(sketch, "E210.left", {"start": v(-16.56, -29.07) * mm, "end": v(-16.56, -43.3) * mm});
            skLineSegment(sketch, "E210.right", {"start": v(4.45, -29.07) * mm, "end": v(4.45, -43.3) * mm});
            skSolve(sketch);
        }
        {
            var Q0;
            Q0 = qSketchRegion(id + "F52", true);
            extrude(context, id + "F53", {"entities" : qUnion([Q0]), "operationType" : NewBodyOperationType.ADD, "depth" : 6 * mm});
        }
    });
